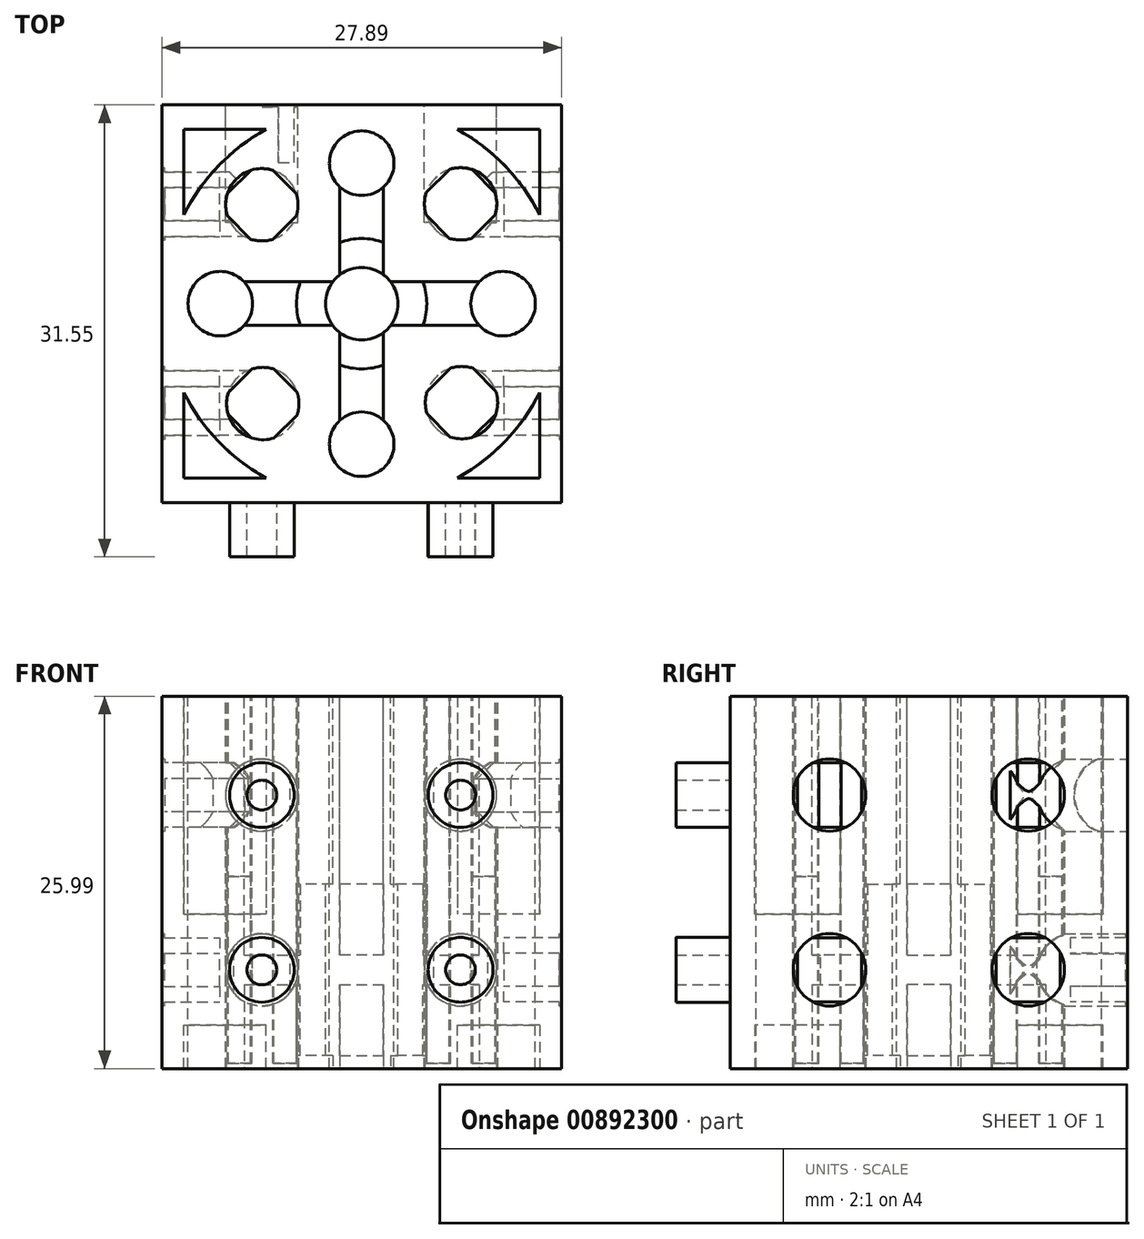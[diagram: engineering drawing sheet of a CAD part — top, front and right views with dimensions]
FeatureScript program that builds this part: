
annotation { "Feature Type Name" : "Feature", "Feature Type Description" : "" }
export const myFeature = defineFeature(function(context is Context, id is Id, definition is map)
    precondition{}
    {
        {
            var Q0;
            Q0=qCreatedBy(makeId("Top.planeOp"),FACE);
            var sketch = newSketch(context, id + "F0", { "sketchPlane" : qUnion([Q0])});
            skLineSegment(sketch, "E0.bottom", {"start": v(-12.61, 9.27) * mm, "end": v(15.28, 9.27) * mm});
            skLineSegment(sketch, "E0.top", {"start": v(-12.61, -18.5) * mm, "end": v(15.28, -18.5) * mm});
            skLineSegment(sketch, "E0.left", {"start": v(-12.61, 9.27) * mm, "end": v(-12.61, -18.5) * mm});
            skLineSegment(sketch, "E0.right", {"start": v(15.28, 9.27) * mm, "end": v(15.28, -18.5) * mm});
            skSolve(sketch);
        }
        {
            var Q0;
            Q0=qSketchRegion(id+"F0",true);
            extrude(context, id + "F1", {"entities" : qUnion([Q0]), "depth" : 13.8 * mm, "offsetDistance" : 25.4 * mm});
        }
        {
            var Q0;
            Q0=makeQuery(id+"F1.opExtrude","CAP_FACE",FACE,{"disambiguationData":[OSD([sQuery(id+"F0.wireOp",EDGE,"E0.bottom"),sQuery(id+"F0.wireOp",EDGE,"E0.top"),sQuery(id+"F0.wireOp",EDGE,"E0.left"),sQuery(id+"F0.wireOp",EDGE,"E0.right")])],"isStart":false});
            var sketch = newSketch(context, id + "F2", { "sketchPlane" : qUnion([Q0])});
            skLineSegment(sketch, "E1", {"start": v(1.33, 9.27) * mm, "end": v(1.33, -18.5) * mm, "construction": true});
            skLineSegment(sketch, "E2", {"start": v(-12.61, -4.61) * mm, "end": v(15.28, -4.61) * mm, "construction": true});
            skLineSegment(sketch, "E3.bottom", {"start": v(13.75, 7.56) * mm, "end": v(-11.09, 7.56) * mm});
            skLineSegment(sketch, "E3.top", {"start": v(13.75, -16.78) * mm, "end": v(-11.09, -16.78) * mm});
            skLineSegment(sketch, "E3.left", {"start": v(13.75, 7.56) * mm, "end": v(13.75, -16.78) * mm});
            skLineSegment(sketch, "E3.right", {"start": v(-11.09, 7.56) * mm, "end": v(-11.09, -16.78) * mm});
            skPoint(sketch, "E3.middle", {"position": v(1.33, -4.61) * mm});
            skSolve(sketch);
        }
        {
            var Q0;
            Q0=qSketchRegion(id+"F2",true);
            extrude(context, id + "F3", {"entities" : qUnion([Q0]), "operationType" : NewBodyOperationType.REMOVE, "oppositeDirection" : true, "depth" : 3.02 * mm, "offsetDistance" : 25.4 * mm});
        }
        {
            var Q0;
            Q0=makeQuery(id+"F1.opExtrude","CAP_FACE",FACE,{"disambiguationData":[OSD([sQuery(id+"F0.wireOp",EDGE,"E0.bottom"),sQuery(id+"F0.wireOp",EDGE,"E0.top"),sQuery(id+"F0.wireOp",EDGE,"E0.left"),sQuery(id+"F0.wireOp",EDGE,"E0.right")])],"isStart":true});
            var sketch = newSketch(context, id + "F4", { "sketchPlane" : qUnion([Q0])});
            skLineSegment(sketch, "E4.bottom", {"start": v(-11.09, -7.56) * mm, "end": v(13.75, -7.56) * mm});
            skLineSegment(sketch, "E4.top", {"start": v(-11.09, 16.78) * mm, "end": v(13.75, 16.78) * mm});
            skLineSegment(sketch, "E4.left", {"start": v(-11.09, -7.56) * mm, "end": v(-11.09, 16.78) * mm});
            skLineSegment(sketch, "E4.right", {"start": v(13.75, -7.56) * mm, "end": v(13.75, 16.78) * mm});
            skSolve(sketch);
        }
        {
            var Q0;
            Q0=makeQuery(id+"F4.imprint","IMPRINT",FACE,{"disambiguationData":[TD([[makeQuery(id+"F4.imprint","IMPRINT",EDGE,{"derivedFrom":sQuery(id+"F4.wireOp",EDGE,"E4.bottom")}),1.0]])]});
            extrude(context, id + "F5", {"entities" : qUnion([Q0]), "operationType" : NewBodyOperationType.REMOVE, "oppositeDirection" : true, "depth" : 3.02 * mm, "offsetDistance" : 25.4 * mm});
        }
        {
            var Q0;
            Q0=makeQuery(id+"F5.boolean.opBoolean","COPY",FACE,{"derivedFrom":makeQuery(id+"F5.opExtrude","CAP_FACE",FACE,{"disambiguationData":[OSD([sQuery(id+"F4.wireOp",EDGE,"E4.bottom"),sQuery(id+"F4.wireOp",EDGE,"E4.top"),sQuery(id+"F4.wireOp",EDGE,"E4.left"),sQuery(id+"F4.wireOp",EDGE,"E4.right")])],"isStart":false})});
            var sketch = newSketch(context, id + "F6", { "sketchPlane" : qUnion([Q0])});
            skCircle(sketch, "E5", {"center": v(1.33, 4.61) * mm, "radius": 13.88 * mm});
            skLineSegment(sketch, "E6", {"start": v(1.33, -7.56) * mm, "end": v(1.33, 16.78) * mm, "construction": true});
            skPoint(sketch, "E6.startSnap0", {"position": v(1.33, -7.56) * mm});
            skSolve(sketch);
        }
        {
            var Q0;
            {var subQ0=sQuery(id+"F6.wireOp",EDGE,"E5");var subQ1=makeQuery(id+"F5.boolean.opBoolean","COPY",EDGE,{"derivedFrom":makeQuery(id+"F5.opExtrude","CAP_EDGE",EDGE,{"disambiguationData":[OSD([sQuery(id+"F4.wireOp",EDGE,"E4.top")])],"isStart":false})});var subQ2=makeQuery(id+"F6.imprint","INTERSECT",VERTEX,{"disambiguationData":[OD(0.0)],"derivedFrom":[subQ1,subQ0]});Q0=makeQuery(id+"F6.imprint","IMPRINT",FACE,{"disambiguationData":[TD([[makeQuery(id+"F6.imprint","IMPRINT",EDGE,{"disambiguationData":[TD([[subQ2,-1.0]])],"derivedFrom":subQ0}),1.0]])]});}
            var Q1;
            {var subQ0=sQuery(id+"F6.wireOp",EDGE,"E5");var subQ1=makeQuery(id+"F5.boolean.opBoolean","COPY",EDGE,{"derivedFrom":makeQuery(id+"F5.opExtrude","CAP_EDGE",EDGE,{"disambiguationData":[OSD([sQuery(id+"F4.wireOp",EDGE,"E4.left")])],"isStart":false})});var subQ2=makeQuery(id+"F6.imprint","INTERSECT",VERTEX,{"disambiguationData":[OD(0.0)],"derivedFrom":[subQ1,subQ0]});Q1=makeQuery(id+"F6.imprint","IMPRINT",FACE,{"disambiguationData":[TD([[makeQuery(id+"F6.imprint","IMPRINT",EDGE,{"disambiguationData":[TD([[subQ2,-1.0]])],"derivedFrom":subQ0}),1.0]])]});}
            var Q2;
            {var subQ0=sQuery(id+"F6.wireOp",EDGE,"E5");var subQ1=makeQuery(id+"F5.boolean.opBoolean","COPY",EDGE,{"derivedFrom":makeQuery(id+"F5.opExtrude","CAP_EDGE",EDGE,{"disambiguationData":[OSD([sQuery(id+"F4.wireOp",EDGE,"E4.bottom")])],"isStart":false})});var subQ2=makeQuery(id+"F6.imprint","INTERSECT",VERTEX,{"disambiguationData":[OD(0.0)],"derivedFrom":[subQ1,subQ0]});Q2=makeQuery(id+"F6.imprint","IMPRINT",FACE,{"disambiguationData":[TD([[makeQuery(id+"F6.imprint","IMPRINT",EDGE,{"disambiguationData":[TD([[subQ2,-1.0]])],"derivedFrom":subQ0}),1.0]])]});}
            var Q3;
            {var subQ0=sQuery(id+"F6.wireOp",EDGE,"E5");var subQ1=makeQuery(id+"F5.boolean.opBoolean","COPY",EDGE,{"derivedFrom":makeQuery(id+"F5.opExtrude","CAP_EDGE",EDGE,{"disambiguationData":[OSD([sQuery(id+"F4.wireOp",EDGE,"E4.right")])],"isStart":false})});var subQ2=makeQuery(id+"F6.imprint","INTERSECT",VERTEX,{"disambiguationData":[OD(0.0)],"derivedFrom":[subQ1,subQ0]});Q3=makeQuery(id+"F6.imprint","IMPRINT",FACE,{"disambiguationData":[TD([[makeQuery(id+"F6.imprint","IMPRINT",EDGE,{"disambiguationData":[TD([[subQ2,1.0]])],"derivedFrom":subQ0}),1.0]])]});}
            var Q4;
            {var subQ0=sQuery(id+"F6.wireOp",EDGE,"E5");var subQ8=makeQuery(id+"F5.boolean.opBoolean","COPY",EDGE,{"derivedFrom":makeQuery(id+"F5.opExtrude","CAP_EDGE",EDGE,{"disambiguationData":[OSD([sQuery(id+"F4.wireOp",EDGE,"E4.top")])],"isStart":false})});var subQ11=makeQuery(id+"F6.imprint","INTERSECT",VERTEX,{"disambiguationData":[OD(0.0)],"derivedFrom":[subQ8,subQ0]});Q4=makeQuery(id+"F6.imprint","IMPRINT",FACE,{"disambiguationData":[TD([[makeQuery(id+"F6.imprint","IMPRINT",EDGE,{"disambiguationData":[TD([[subQ11,1.0]])],"derivedFrom":subQ0}),1.0]])]});}
            extrude(context, id + "F7", {"entities" : qUnion([Q0, Q1, Q2, Q3, Q4]), "operationType" : NewBodyOperationType.ADD, "depth" : 3.02 * mm, "offsetDistance" : 25.4 * mm});
        }
        {
            var Q0;
            Q0=makeQuery(id+"F3.boolean.opBoolean","COPY",FACE,{"derivedFrom":makeQuery(id+"F3.opExtrude","CAP_FACE",FACE,{"disambiguationData":[OSD([sQuery(id+"F2.wireOp",EDGE,"E3.bottom"),sQuery(id+"F2.wireOp",EDGE,"E3.top"),sQuery(id+"F2.wireOp",EDGE,"E3.left"),sQuery(id+"F2.wireOp",EDGE,"E3.right")])],"isStart":false})});
            var sketch = newSketch(context, id + "F8", { "sketchPlane" : qUnion([Q0])});
            skLineSegment(sketch, "E7", {"start": v(1.33, 7.56) * mm, "end": v(1.33, -16.78) * mm, "construction": true});
            skCircle(sketch, "E8", {"center": v(1.33, -4.61) * mm, "radius": 13.88 * mm});
            skSolve(sketch);
        }
        {
            var Q0;
            Q0=qSketchRegion(id+"F8",true);
            extrude(context, id + "F9", {"entities" : qUnion([Q0]), "operationType" : NewBodyOperationType.ADD, "depth" : 3.02 * mm, "offsetDistance" : 25.4 * mm});
        }
        {
            var Q0;
            Q0=makeQuery(id+"F9.boolean.opBoolean","MERGE",FACE,{"derivedFrom":[makeQuery(id+"F1.opExtrude","CAP_FACE",FACE,{"disambiguationData":[OSD([sQuery(id+"F0.wireOp",EDGE,"E0.bottom"),sQuery(id+"F0.wireOp",EDGE,"E0.top"),sQuery(id+"F0.wireOp",EDGE,"E0.left"),sQuery(id+"F0.wireOp",EDGE,"E0.right")])],"isStart":false}),makeQuery(id+"F9.opExtrude","CAP_FACE",FACE,{"disambiguationData":[OSD([sQuery(id+"F8.wireOp",EDGE,"E8")])],"isStart":false})]});
            var sketch = newSketch(context, id + "F10", { "sketchPlane" : qUnion([Q0])});
            skLineSegment(sketch, "E9", {"start": v(-12.61, -4.61) * mm, "end": v(15.28, -4.61) * mm, "construction": true});
            skLineSegment(sketch, "E10", {"start": v(1.33, 9.27) * mm, "end": v(1.33, -18.5) * mm, "construction": true});
            skCircle(sketch, "E11", {"center": v(1.33, -4.61) * mm, "radius": 2.53 * mm});
            skCircle(sketch, "E12", {"center": v(1.33, -14.42) * mm, "radius": 2.25 * mm});
            skCircle(sketch, "E13", {"center": v(1.33, 5.2) * mm, "radius": 2.25 * mm});
            skCircle(sketch, "E14", {"center": v(-8.54, -4.61) * mm, "radius": 2.25 * mm});
            skCircle(sketch, "E15", {"center": v(11.2, -4.61) * mm, "radius": 2.25 * mm});
            skCircle(sketch, "E16", {"center": v(-5.64, 2.3) * mm, "radius": 2.53 * mm});
            skCircle(sketch, "E17.1.0", {"center": v(-5.57, -11.58) * mm, "radius": 2.53 * mm});
            skCircle(sketch, "E17.2.0", {"center": v(8.3, -11.52) * mm, "radius": 2.53 * mm});
            skCircle(sketch, "E17.3.0", {"center": v(8.24, 2.36) * mm, "radius": 2.53 * mm});
            skSolve(sketch);
        }
        {
            var Q0;
            Q0=qSketchRegion(id+"F10",true);
            extrude(context, id + "F11", {"entities" : qUnion([Q0]), "operationType" : NewBodyOperationType.REMOVE, "oppositeDirection" : true, "depth" : 25.4 * mm, "offsetDistance" : 25.4 * mm});
        }
        {
            var Q0;
            Q0=makeQuery(id+"F9.boolean.opBoolean","MERGE",FACE,{"derivedFrom":[makeQuery(id+"F1.opExtrude","CAP_FACE",FACE,{"disambiguationData":[OSD([sQuery(id+"F0.wireOp",EDGE,"E0.bottom"),sQuery(id+"F0.wireOp",EDGE,"E0.top"),sQuery(id+"F0.wireOp",EDGE,"E0.left"),sQuery(id+"F0.wireOp",EDGE,"E0.right")])],"isStart":false}),makeQuery(id+"F9.opExtrude","CAP_FACE",FACE,{"disambiguationData":[OSD([sQuery(id+"F8.wireOp",EDGE,"E8")])],"isStart":false})]});
            var sketch = newSketch(context, id + "F12", { "sketchPlane" : qUnion([Q0])});
            skLineSegment(sketch, "E18", {"start": v(-12.61, -4.61) * mm, "end": v(15.28, -4.61) * mm, "construction": true});
            skLineSegment(sketch, "E19", {"start": v(1.33, 9.27) * mm, "end": v(1.33, -18.5) * mm, "construction": true});
            skLineSegment(sketch, "E20", {"start": v(-6.88, -3.09) * mm, "end": v(9.55, -3.09) * mm});
            skLineSegment(sketch, "E21", {"start": v(-6.88, -6.14) * mm, "end": v(9.55, -6.14) * mm});
            skLineSegment(sketch, "E22", {"start": v(-0.19, 3.54) * mm, "end": v(-0.19, -12.76) * mm});
            skLineSegment(sketch, "E23", {"start": v(2.86, -12.76) * mm, "end": v(2.86, 3.54) * mm});
            skLineSegment(sketch, "E24", {"start": v(-0.19, -7.96) * mm, "end": v(2.86, -7.96) * mm, "construction": true});
            skPoint(sketch, "E25", {"position": v(1.33, -7.96) * mm});
            skLineSegment(sketch, "E26", {"start": v(-2, -3.09) * mm, "end": v(-2, -6.14) * mm, "construction": true});
            skPoint(sketch, "E27", {"position": v(-2, -4.61) * mm});
            skSolve(sketch);
        }
        {
            var Q0;
            {var subQ0=sQuery(id+"F12.wireOp",EDGE,"E22");var subQ1=makeQuery(id+"F11.boolean.opBoolean","COPY",EDGE,{"derivedFrom":makeQuery(id+"F11.opExtrude","CAP_EDGE",EDGE,{"disambiguationData":[OSD([sQuery(id+"F10.wireOp",EDGE,"E13")])],"isStart":true})});var subQ2=makeQuery(id+"F12.imprint","INTERSECT",VERTEX,{"derivedFrom":[subQ1,subQ0]});Q0=makeQuery(id+"F12.imprint","IMPRINT",FACE,{"disambiguationData":[TD([[makeQuery(id+"F12.imprint","IMPRINT",EDGE,{"disambiguationData":[TD([[subQ2,-1.0]])],"derivedFrom":subQ0}),1.0]])]});}
            var Q1;
            {var subQ0=sQuery(id+"F12.wireOp",EDGE,"E22");var subQ1=makeQuery(id+"F11.boolean.opBoolean","COPY",EDGE,{"derivedFrom":makeQuery(id+"F11.opExtrude","CAP_EDGE",EDGE,{"disambiguationData":[OSD([sQuery(id+"F10.wireOp",EDGE,"E12")])],"isStart":true})});var subQ2=makeQuery(id+"F12.imprint","INTERSECT",VERTEX,{"derivedFrom":[subQ1,subQ0]});Q1=makeQuery(id+"F12.imprint","IMPRINT",FACE,{"disambiguationData":[TD([[makeQuery(id+"F12.imprint","IMPRINT",EDGE,{"disambiguationData":[TD([[subQ2,1.0]])],"derivedFrom":subQ0}),1.0]])]});}
            var Q2;
            {var subQ0=sQuery(id+"F12.wireOp",EDGE,"E20");var subQ1=makeQuery(id+"F11.boolean.opBoolean","COPY",EDGE,{"derivedFrom":makeQuery(id+"F11.opExtrude","CAP_EDGE",EDGE,{"disambiguationData":[OSD([sQuery(id+"F10.wireOp",EDGE,"E14")])],"isStart":true})});var subQ2=makeQuery(id+"F12.imprint","INTERSECT",VERTEX,{"derivedFrom":[subQ1,subQ0]});Q2=makeQuery(id+"F12.imprint","IMPRINT",FACE,{"disambiguationData":[TD([[makeQuery(id+"F12.imprint","IMPRINT",EDGE,{"disambiguationData":[TD([[subQ2,-1.0]])],"derivedFrom":subQ0}),-1.0]])]});}
            var Q3;
            {var subQ0=sQuery(id+"F12.wireOp",EDGE,"E20");var subQ1=makeQuery(id+"F11.boolean.opBoolean","COPY",EDGE,{"derivedFrom":makeQuery(id+"F11.opExtrude","CAP_EDGE",EDGE,{"disambiguationData":[OSD([sQuery(id+"F10.wireOp",EDGE,"E15")])],"isStart":true})});var subQ2=makeQuery(id+"F12.imprint","INTERSECT",VERTEX,{"derivedFrom":[subQ1,subQ0]});Q3=makeQuery(id+"F12.imprint","IMPRINT",FACE,{"disambiguationData":[TD([[makeQuery(id+"F12.imprint","IMPRINT",EDGE,{"disambiguationData":[TD([[subQ2,1.0]])],"derivedFrom":subQ0}),-1.0]])]});}
            extrude(context, id + "F13", {"entities" : qUnion([Q0, Q1, Q2, Q3]), "operationType" : NewBodyOperationType.REMOVE, "oppositeDirection" : true, "depth" : 5.87 * mm, "offsetDistance" : 25.4 * mm});
        }
        {
            var Q0;
            Q0=makeQuery(id+"F7.boolean.opBoolean","MERGE",FACE,{"derivedFrom":[makeQuery(id+"F1.opExtrude","CAP_FACE",FACE,{"disambiguationData":[OSD([sQuery(id+"F0.wireOp",EDGE,"E0.bottom"),sQuery(id+"F0.wireOp",EDGE,"E0.top"),sQuery(id+"F0.wireOp",EDGE,"E0.left"),sQuery(id+"F0.wireOp",EDGE,"E0.right")])],"isStart":true}),makeQuery(id+"F7.opExtrude","CAP_FACE",FACE,{"disambiguationData":[OSD([sQuery(id+"F6.wireOp",EDGE,"E5")])],"isStart":false})]});
            var sketch = newSketch(context, id + "F14", { "sketchPlane" : qUnion([Q0])});
            skLineSegment(sketch, "E28.0", {"start": v(2.86, 12.76) * mm, "end": v(2.86, 6.63) * mm});
            skLineSegment(sketch, "E28.1", {"start": v(3.35, 6.14) * mm, "end": v(9.55, 6.14) * mm});
            skLineSegment(sketch, "E28.2", {"start": v(3.35, 3.09) * mm, "end": v(9.55, 3.09) * mm});
            skLineSegment(sketch, "E28.3", {"start": v(2.86, 2.6) * mm, "end": v(2.86, -3.54) * mm});
            skLineSegment(sketch, "E28.4", {"start": v(-0.19, -3.54) * mm, "end": v(-0.19, 2.6) * mm});
            skLineSegment(sketch, "E28.5", {"start": v(-0.19, 6.63) * mm, "end": v(-0.19, 12.76) * mm});
            skLineSegment(sketch, "E28.6", {"start": v(-6.88, 6.14) * mm, "end": v(-0.68, 6.14) * mm});
            skLineSegment(sketch, "E28.7", {"start": v(-6.88, 3.09) * mm, "end": v(-0.68, 3.09) * mm});
            skSolve(sketch);
        }
        {
            var Q0;
            {var subQ0=sQuery(id+"F14.wireOp",EDGE,"E28.6");Q0=makeQuery(id+"F14.imprint","IMPRINT",FACE,{"disambiguationData":[TD([[makeQuery(id+"F14.imprint","IMPRINT",EDGE,{"derivedFrom":subQ0}),-1.0]])]});}
            var Q1;
            {var subQ0=sQuery(id+"F14.wireOp",EDGE,"E28.3");Q1=makeQuery(id+"F14.imprint","IMPRINT",FACE,{"disambiguationData":[TD([[makeQuery(id+"F14.imprint","IMPRINT",EDGE,{"derivedFrom":subQ0}),-1.0]])]});}
            var Q2;
            {var subQ0=sQuery(id+"F14.wireOp",EDGE,"E28.0");Q2=makeQuery(id+"F14.imprint","IMPRINT",FACE,{"disambiguationData":[TD([[makeQuery(id+"F14.imprint","IMPRINT",EDGE,{"derivedFrom":subQ0}),-1.0]])]});}
            var Q3;
            {var subQ0=sQuery(id+"F14.wireOp",EDGE,"E28.1");Q3=makeQuery(id+"F14.imprint","IMPRINT",FACE,{"disambiguationData":[TD([[makeQuery(id+"F14.imprint","IMPRINT",EDGE,{"derivedFrom":subQ0}),-1.0]])]});}
            extrude(context, id + "F15", {"entities" : qUnion([Q0, Q1, Q2, Q3]), "operationType" : NewBodyOperationType.REMOVE, "oppositeDirection" : true, "depth" : 5.87 * mm, "offsetDistance" : 25.4 * mm});
        }
        {
            var Q0;
            Q0=makeQuery(id+"F15.boolean.opBoolean","COPY",FACE,{"derivedFrom":makeQuery(id+"F15.opExtrude","CAP_FACE",FACE,{"disambiguationData":[OSD([sQuery(id+"F0.wireOp",EDGE,"E0.bottom"),sQuery(id+"F0.wireOp",EDGE,"E0.top"),sQuery(id+"F0.wireOp",EDGE,"E0.left"),sQuery(id+"F0.wireOp",EDGE,"E0.right"),sQuery(id+"F6.wireOp",EDGE,"E5"),sQuery(id+"F10.wireOp",EDGE,"E11"),sQuery(id+"F10.wireOp",EDGE,"E13"),sQuery(id+"F14.wireOp",EDGE,"E28.3"),sQuery(id+"F14.wireOp",EDGE,"E28.4")])],"isStart":false})});
            var sketch = newSketch(context, id + "F16", { "sketchPlane" : qUnion([Q0])});
            skCircle(sketch, "E29", {"center": v(1.33, 4.61) * mm, "radius": 4.55 * mm});
            skCircle(sketch, "E30", {"center": v(1.33, 4.61) * mm, "radius": 2.53 * mm});
            skSolve(sketch);
        }
        {
            var Q0;
            {var subQ5=sQuery(id+"F16.wireOp",EDGE,"E30");Q0=makeQuery(id+"F16.imprint","IMPRINT",FACE,{"disambiguationData":[TD([[makeQuery(id+"F16.imprint","IMPRINT",EDGE,{"disambiguationData":[OD(1.0)],"derivedFrom":subQ5}),-1.0]])]});}
            var Q1;
            {var subQ5=sQuery(id+"F16.wireOp",EDGE,"E30");Q1=makeQuery(id+"F16.imprint","IMPRINT",FACE,{"disambiguationData":[TD([[makeQuery(id+"F16.imprint","IMPRINT",EDGE,{"disambiguationData":[OD(0.0)],"derivedFrom":subQ5}),1.0]])]});}
            extrude(context, id + "F17", {"entities" : qUnion([Q0, Q1]), "operationType" : NewBodyOperationType.ADD, "depth" : 4.95 * mm, "offsetDistance" : 25.4 * mm});
        }
        {
            var Q0;
            Q0=makeQuery(id+"F13.boolean.opBoolean","COPY",FACE,{"derivedFrom":makeQuery(id+"F13.opExtrude","CAP_FACE",FACE,{"disambiguationData":[OSD([sQuery(id+"F10.wireOp",EDGE,"E11"),sQuery(id+"F10.wireOp",EDGE,"E12"),sQuery(id+"F12.wireOp",EDGE,"E22"),sQuery(id+"F12.wireOp",EDGE,"E23")])],"isStart":false})});
            var sketch = newSketch(context, id + "F18", { "sketchPlane" : qUnion([Q0])});
            skCircle(sketch, "E31", {"center": v(1.33, -4.61) * mm, "radius": 4.55 * mm});
            skCircle(sketch, "E32", {"center": v(1.33, -4.61) * mm, "radius": 2.53 * mm});
            skSolve(sketch);
        }
        {
            var Q0;
            {var subQ0=sQuery(id+"F18.wireOp",EDGE,"E31");var subQ1=sQuery(id+"F12.wireOp",EDGE,"E22");var subQ2=makeQuery(id+"F11.boolean.opBoolean","COPY",EDGE,{"derivedFrom":makeQuery(id+"F11.opExtrude","CAP_EDGE",EDGE,{"disambiguationData":[OSD([sQuery(id+"F10.wireOp",EDGE,"E12")])],"isStart":true})});var subQ4=makeQuery(id+"F13.boolean.opBoolean","COPY",EDGE,{"derivedFrom":makeQuery(id+"F13.opExtrude","CAP_EDGE",EDGE,{"disambiguationData":[OSD([subQ1]),TDD([makeQuery(id+"F12.imprint","IMPRINT",EDGE,{"disambiguationData":[TD([[makeQuery(id+"F12.imprint","INTERSECT",VERTEX,{"derivedFrom":[subQ2,subQ1]}),1.0]])],"derivedFrom":subQ1})])],"isStart":false})});var subQ5=makeQuery(id+"F18.imprint","INTERSECT",VERTEX,{"derivedFrom":[subQ4,subQ0]});Q0=makeQuery(id+"F18.imprint","IMPRINT",FACE,{"disambiguationData":[TD([[makeQuery(id+"F18.imprint","IMPRINT",EDGE,{"disambiguationData":[TD([[subQ5,1.0]])],"derivedFrom":subQ0}),1.0]])]});}
            var Q1;
            {var subQ0=sQuery(id+"F18.wireOp",EDGE,"E31");var subQ1=sQuery(id+"F12.wireOp",EDGE,"E22");var subQ2=makeQuery(id+"F11.boolean.opBoolean","COPY",EDGE,{"derivedFrom":makeQuery(id+"F11.opExtrude","CAP_EDGE",EDGE,{"disambiguationData":[OSD([sQuery(id+"F10.wireOp",EDGE,"E12")])],"isStart":true})});var subQ4=makeQuery(id+"F13.boolean.opBoolean","COPY",EDGE,{"derivedFrom":makeQuery(id+"F13.opExtrude","CAP_EDGE",EDGE,{"disambiguationData":[OSD([subQ1]),TDD([makeQuery(id+"F12.imprint","IMPRINT",EDGE,{"disambiguationData":[TD([[makeQuery(id+"F12.imprint","INTERSECT",VERTEX,{"derivedFrom":[subQ2,subQ1]}),1.0]])],"derivedFrom":subQ1})])],"isStart":false})});var subQ5=makeQuery(id+"F18.imprint","INTERSECT",VERTEX,{"derivedFrom":[subQ4,subQ0]});Q1=makeQuery(id+"F18.imprint","IMPRINT",FACE,{"disambiguationData":[TD([[makeQuery(id+"F18.imprint","IMPRINT",EDGE,{"disambiguationData":[TD([[subQ5,-1.0]])],"derivedFrom":subQ0}),1.0]])]});}
            extrude(context, id + "F19", {"entities" : qUnion([Q0, Q1]), "operationType" : NewBodyOperationType.ADD, "depth" : 4.95 * mm, "offsetDistance" : 25.4 * mm});
        }
        {
            var Q0;
            Q0=makeQuery(id+"F1.opExtrude","SWEPT_FACE",FACE,{"disambiguationData":[OSD([sQuery(id+"F0.wireOp",EDGE,"E0.top")])]});
            var sketch = newSketch(context, id + "F20", { "sketchPlane" : qUnion([Q0])});
            skLineSegment(sketch, "E33", {"start": v(15.28, 6.9) * mm, "end": v(-12.61, 6.9) * mm, "construction": true});
            skCircle(sketch, "E34", {"center": v(8.23, 6.9) * mm, "radius": 2.26 * mm});
            skCircle(sketch, "E35", {"center": v(-5.64, 6.9) * mm, "radius": 2.26 * mm});
            skLineSegment(sketch, "E36", {"start": v(1.33, 0) * mm, "end": v(1.33, 13.8) * mm, "construction": true});
            skPoint(sketch, "E37", {"position": v(1.33, 6.9) * mm});
            skLineSegment(sketch, "E38", {"start": v(1.33, 0) * mm, "end": v(15.28, 0) * mm, "construction": true});
            skLineSegment(sketch, "E39", {"start": v(15.28, 0) * mm, "end": v(8.3, 0) * mm});
            skLineSegment(sketch, "E40", {"start": v(8.3, 0) * mm, "end": v(8.3, 13.8) * mm, "construction": true});
            skLineSegment(sketch, "E41", {"start": v(1.33, 0) * mm, "end": v(-12.61, 0) * mm, "construction": true});
            skLineSegment(sketch, "E42", {"start": v(-5.64, 0) * mm, "end": v(-5.64, 13.8) * mm, "construction": true});
            skCircle(sketch, "E43", {"center": v(8.23, 6.9) * mm, "radius": 1.04 * mm});
            skCircle(sketch, "E44", {"center": v(-5.64, 6.9) * mm, "radius": 1.04 * mm});
            skLineSegment(sketch, "E45.0", {"start": v(-12.61, 13.8) * mm, "end": v(-12.61, 0) * mm});
            skSolve(sketch);
        }
        {
            var Q0;
            Q0=makeQuery(id+"F20.imprint","IMPRINT",FACE,{"disambiguationData":[TD([[makeQuery(id+"F20.imprint","IMPRINT",EDGE,{"derivedFrom":sQuery(id+"F20.wireOp",EDGE,"E34")}),1.0]])]});
            var Q1;
            Q1=makeQuery(id+"F20.imprint","IMPRINT",FACE,{"disambiguationData":[TD([[makeQuery(id+"F20.imprint","IMPRINT",EDGE,{"derivedFrom":sQuery(id+"F20.wireOp",EDGE,"E35")}),1.0]])]});
            extrude(context, id + "F21", {"entities" : qUnion([Q0, Q1]), "operationType" : NewBodyOperationType.ADD, "depth" : 3.78 * mm, "offsetDistance" : 25.4 * mm});
        }
        {
            var Q0;
            Q0=makeQuery(id+"F1.opExtrude","SWEPT_FACE",FACE,{"disambiguationData":[OSD([sQuery(id+"F0.wireOp",EDGE,"E0.bottom")])]});
            var sketch = newSketch(context, id + "F22", { "sketchPlane" : qUnion([Q0])});
            skCircle(sketch, "E46.0", {"center": v(-8.23, 6.9) * mm, "radius": 2.26 * mm, "construction": true});
            skCircle(sketch, "E46.1", {"center": v(5.64, 6.9) * mm, "radius": 2.26 * mm, "construction": true});
            skCircle(sketch, "E47", {"center": v(-8.23, 6.9) * mm, "radius": 2.53 * mm});
            skCircle(sketch, "E48", {"center": v(5.64, 6.9) * mm, "radius": 2.53 * mm});
            skSolve(sketch);
        }
        {
            var Q0;
            Q0=qSketchRegion(id+"F22",true);
            extrude(context, id + "F23", {"entities" : qUnion([Q0]), "operationType" : NewBodyOperationType.REMOVE, "oppositeDirection" : true, "depth" : 4 * mm, "offsetDistance" : 25.4 * mm});
        }
        {
            var Q0;
            Q0=makeQuery(id+"F1.opExtrude","SWEPT_FACE",FACE,{"disambiguationData":[OSD([sQuery(id+"F0.wireOp",EDGE,"E0.right")])]});
            var sketch = newSketch(context, id + "F24", { "sketchPlane" : qUnion([Q0])});
            skLineSegment(sketch, "E49", {"start": v(9.27, 6.9) * mm, "end": v(-18.5, 6.9) * mm, "construction": true});
            skLineSegment(sketch, "E50", {"start": v(-4.61, 13.8) * mm, "end": v(-4.61, 0) * mm});
            skLineSegment(sketch, "E51", {"start": v(-4.61, 13.8) * mm, "end": v(9.27, 13.8) * mm, "construction": true});
            skLineSegment(sketch, "E52", {"start": v(-4.61, 13.8) * mm, "end": v(-18.5, 13.8) * mm, "construction": true});
            skLineSegment(sketch, "E53", {"start": v(-11.55, 13.8) * mm, "end": v(-11.55, 0) * mm, "construction": true});
            skLineSegment(sketch, "E54", {"start": v(2.33, 13.8) * mm, "end": v(2.33, 0) * mm, "construction": true});
            skPoint(sketch, "E55", {"position": v(-11.55, 6.9) * mm});
            skPoint(sketch, "E56", {"position": v(2.33, 6.9) * mm});
            skCircle(sketch, "E57", {"center": v(-11.55, 6.9) * mm, "radius": 2.53 * mm});
            skCircle(sketch, "E58", {"center": v(2.33, 6.9) * mm, "radius": 2.53 * mm});
            skSolve(sketch);
        }
        {
            var Q0;
            Q0=qSketchRegion(id+"F24",true);
            extrude(context, id + "F25", {"entities" : qUnion([Q0]), "operationType" : NewBodyOperationType.REMOVE, "oppositeDirection" : true, "depth" : 4 * mm, "offsetDistance" : 25.4 * mm});
        }
        {
            var Q0;
            Q0=makeQuery(id+"F1.opExtrude","SWEPT_FACE",FACE,{"disambiguationData":[OSD([sQuery(id+"F0.wireOp",EDGE,"E0.left")])]});
            var sketch = newSketch(context, id + "F26", { "sketchPlane" : qUnion([Q0])});
            skCircle(sketch, "E59.0", {"center": v(-2.33, 6.9) * mm, "radius": 2.53 * mm});
            skCircle(sketch, "E59.1", {"center": v(11.55, 6.9) * mm, "radius": 2.53 * mm});
            skSolve(sketch);
        }
        {
            var Q0;
            Q0=qSketchRegion(id+"F26",true);
            extrude(context, id + "F27", {"entities" : qUnion([Q0]), "operationType" : NewBodyOperationType.REMOVE, "oppositeDirection" : true, "depth" : 4 * mm, "offsetDistance" : 25.4 * mm});
        }
        {
            var Q0;
            Q0=makeQuery(id+"F23.boolean.opBoolean","COPY",FACE,{"derivedFrom":makeQuery(id+"F23.opExtrude","CAP_FACE",FACE,{"disambiguationData":[OSD([sQuery(id+"F22.wireOp",EDGE,"E47")])],"isStart":false})});
            var sketch = newSketch(context, id + "F28", { "sketchPlane" : qUnion([Q0])});
            skLineSegment(sketch, "E60.bottom", {"start": v(-5.98, 9.14) * mm, "end": v(-10.48, 9.14) * mm});
            skLineSegment(sketch, "E60.top", {"start": v(-5.98, 4.65) * mm, "end": v(-10.48, 4.65) * mm});
            skLineSegment(sketch, "E60.left", {"start": v(-5.98, 9.14) * mm, "end": v(-5.98, 4.65) * mm});
            skLineSegment(sketch, "E60.right", {"start": v(-10.48, 9.14) * mm, "end": v(-10.48, 4.65) * mm});
            skPoint(sketch, "E60.middle", {"position": v(-8.23, 6.9) * mm});
            skLineSegment(sketch, "E61.bottom", {"start": v(7.89, 9.14) * mm, "end": v(3.4, 9.14) * mm});
            skLineSegment(sketch, "E61.top", {"start": v(7.89, 4.65) * mm, "end": v(3.4, 4.65) * mm});
            skLineSegment(sketch, "E61.left", {"start": v(7.89, 9.14) * mm, "end": v(7.89, 4.65) * mm});
            skLineSegment(sketch, "E61.right", {"start": v(3.4, 9.14) * mm, "end": v(3.4, 4.65) * mm});
            skPoint(sketch, "E61.middle", {"position": v(5.64, 6.9) * mm});
            skCircle(sketch, "E62.0", {"center": v(-8.23, 6.9) * mm, "radius": 2.53 * mm});
            skCircle(sketch, "E63.0", {"center": v(5.64, 6.9) * mm, "radius": 2.53 * mm});
            skSolve(sketch);
        }
        {
            var Q0;
            {var subQ0=sQuery(id+"F28.wireOp",EDGE,"E62.0");var subQ1=sQuery(id+"F28.wireOp",EDGE,"E60.right");var subQ2=makeQuery(id+"F28.imprint","INTERSECT",VERTEX,{"disambiguationData":[OD(0.0)],"derivedFrom":[subQ1,subQ0]});Q0=makeQuery(id+"F28.imprint","IMPRINT",FACE,{"disambiguationData":[TD([[makeQuery(id+"F28.imprint","IMPRINT",EDGE,{"disambiguationData":[TD([[subQ2,-1.0]])],"derivedFrom":subQ1}),-1.0]])]});}
            var Q1;
            {var subQ0=sQuery(id+"F28.wireOp",EDGE,"E62.0");var subQ1=sQuery(id+"F28.wireOp",EDGE,"E60.top");var subQ2=makeQuery(id+"F28.imprint","INTERSECT",VERTEX,{"disambiguationData":[OD(0.0)],"derivedFrom":[subQ1,subQ0]});Q1=makeQuery(id+"F28.imprint","IMPRINT",FACE,{"disambiguationData":[TD([[makeQuery(id+"F28.imprint","IMPRINT",EDGE,{"disambiguationData":[TD([[subQ2,-1.0]])],"derivedFrom":subQ1}),1.0]])]});}
            var Q2;
            {var subQ0=sQuery(id+"F28.wireOp",EDGE,"E62.0");var subQ1=sQuery(id+"F28.wireOp",EDGE,"E60.left");var subQ2=makeQuery(id+"F28.imprint","INTERSECT",VERTEX,{"disambiguationData":[OD(0.0)],"derivedFrom":[subQ1,subQ0]});Q2=makeQuery(id+"F28.imprint","IMPRINT",FACE,{"disambiguationData":[TD([[makeQuery(id+"F28.imprint","IMPRINT",EDGE,{"disambiguationData":[TD([[subQ2,-1.0]])],"derivedFrom":subQ1}),1.0]])]});}
            var Q3;
            {var subQ0=sQuery(id+"F28.wireOp",EDGE,"E62.0");var subQ1=sQuery(id+"F28.wireOp",EDGE,"E60.bottom");var subQ2=makeQuery(id+"F28.imprint","INTERSECT",VERTEX,{"disambiguationData":[OD(0.0)],"derivedFrom":[subQ1,subQ0]});Q3=makeQuery(id+"F28.imprint","IMPRINT",FACE,{"disambiguationData":[TD([[makeQuery(id+"F28.imprint","IMPRINT",EDGE,{"disambiguationData":[TD([[subQ2,-1.0]])],"derivedFrom":subQ1}),-1.0]])]});}
            var Q4;
            {var subQ0=sQuery(id+"F28.wireOp",EDGE,"E63.0");var subQ1=sQuery(id+"F28.wireOp",EDGE,"E61.bottom");var subQ2=makeQuery(id+"F28.imprint","INTERSECT",VERTEX,{"disambiguationData":[OD(0.0)],"derivedFrom":[subQ1,subQ0]});Q4=makeQuery(id+"F28.imprint","IMPRINT",FACE,{"disambiguationData":[TD([[makeQuery(id+"F28.imprint","IMPRINT",EDGE,{"disambiguationData":[TD([[subQ2,-1.0]])],"derivedFrom":subQ1}),-1.0]])]});}
            var Q5;
            {var subQ0=sQuery(id+"F28.wireOp",EDGE,"E63.0");var subQ1=sQuery(id+"F28.wireOp",EDGE,"E61.left");var subQ2=makeQuery(id+"F28.imprint","INTERSECT",VERTEX,{"disambiguationData":[OD(0.0)],"derivedFrom":[subQ1,subQ0]});Q5=makeQuery(id+"F28.imprint","IMPRINT",FACE,{"disambiguationData":[TD([[makeQuery(id+"F28.imprint","IMPRINT",EDGE,{"disambiguationData":[TD([[subQ2,-1.0]])],"derivedFrom":subQ1}),1.0]])]});}
            var Q6;
            {var subQ0=sQuery(id+"F28.wireOp",EDGE,"E63.0");var subQ1=sQuery(id+"F28.wireOp",EDGE,"E61.right");var subQ2=makeQuery(id+"F28.imprint","INTERSECT",VERTEX,{"disambiguationData":[OD(0.0)],"derivedFrom":[subQ1,subQ0]});Q6=makeQuery(id+"F28.imprint","IMPRINT",FACE,{"disambiguationData":[TD([[makeQuery(id+"F28.imprint","IMPRINT",EDGE,{"disambiguationData":[TD([[subQ2,-1.0]])],"derivedFrom":subQ1}),-1.0]])]});}
            var Q7;
            {var subQ0=sQuery(id+"F28.wireOp",EDGE,"E63.0");var subQ1=sQuery(id+"F28.wireOp",EDGE,"E61.top");var subQ2=makeQuery(id+"F28.imprint","INTERSECT",VERTEX,{"disambiguationData":[OD(0.0)],"derivedFrom":[subQ1,subQ0]});Q7=makeQuery(id+"F28.imprint","IMPRINT",FACE,{"disambiguationData":[TD([[makeQuery(id+"F28.imprint","IMPRINT",EDGE,{"disambiguationData":[TD([[subQ2,-1.0]])],"derivedFrom":subQ1}),1.0]])]});}
            extrude(context, id + "F29", {"entities" : qUnion([Q0, Q1, Q2, Q3, Q4, Q5, Q6, Q7]), "operationType" : NewBodyOperationType.ADD, "depth" : 3.86 * mm, "offsetDistance" : 25.4 * mm});
        }
        {
            var Q0;
            Q0=makeQuery(id+"F25.boolean.opBoolean","COPY",FACE,{"derivedFrom":makeQuery(id+"F25.opExtrude","CAP_FACE",FACE,{"disambiguationData":[OSD([sQuery(id+"F24.wireOp",EDGE,"E57")])],"isStart":false})});
            var sketch = newSketch(context, id + "F30", { "sketchPlane" : qUnion([Q0])});
            skLineSegment(sketch, "E64.bottom", {"start": v(-9.3, 9.14) * mm, "end": v(-13.8, 9.14) * mm});
            skLineSegment(sketch, "E64.top", {"start": v(-9.3, 4.65) * mm, "end": v(-13.8, 4.65) * mm});
            skLineSegment(sketch, "E64.left", {"start": v(-9.3, 9.14) * mm, "end": v(-9.3, 4.65) * mm});
            skLineSegment(sketch, "E64.right", {"start": v(-13.8, 9.14) * mm, "end": v(-13.8, 4.65) * mm});
            skPoint(sketch, "E64.middle", {"position": v(-11.55, 6.9) * mm});
            skLineSegment(sketch, "E65.bottom", {"start": v(4.58, 9.14) * mm, "end": v(0.08, 9.14) * mm});
            skLineSegment(sketch, "E65.top", {"start": v(4.58, 4.65) * mm, "end": v(0.08, 4.65) * mm});
            skLineSegment(sketch, "E65.left", {"start": v(4.58, 9.14) * mm, "end": v(4.58, 4.65) * mm});
            skLineSegment(sketch, "E65.right", {"start": v(0.08, 9.14) * mm, "end": v(0.08, 4.65) * mm});
            skPoint(sketch, "E65.middle", {"position": v(2.33, 6.9) * mm});
            skCircle(sketch, "E66.0", {"center": v(-11.55, 6.9) * mm, "radius": 2.53 * mm});
            skCircle(sketch, "E66.1", {"center": v(2.33, 6.9) * mm, "radius": 2.53 * mm});
            skSolve(sketch);
        }
        {
            var Q0;
            {var subQ0=sQuery(id+"F30.wireOp",EDGE,"E66.0");var subQ1=sQuery(id+"F30.wireOp",EDGE,"E64.bottom");var subQ2=makeQuery(id+"F30.imprint","INTERSECT",VERTEX,{"disambiguationData":[OD(0.0)],"derivedFrom":[subQ1,subQ0]});Q0=makeQuery(id+"F30.imprint","IMPRINT",FACE,{"disambiguationData":[TD([[makeQuery(id+"F30.imprint","IMPRINT",EDGE,{"disambiguationData":[TD([[subQ2,-1.0]])],"derivedFrom":subQ1}),-1.0]])]});}
            var Q1;
            {var subQ0=sQuery(id+"F30.wireOp",EDGE,"E66.0");var subQ1=sQuery(id+"F30.wireOp",EDGE,"E64.right");var subQ2=makeQuery(id+"F30.imprint","INTERSECT",VERTEX,{"disambiguationData":[OD(0.0)],"derivedFrom":[subQ1,subQ0]});Q1=makeQuery(id+"F30.imprint","IMPRINT",FACE,{"disambiguationData":[TD([[makeQuery(id+"F30.imprint","IMPRINT",EDGE,{"disambiguationData":[TD([[subQ2,-1.0]])],"derivedFrom":subQ1}),-1.0]])]});}
            var Q2;
            {var subQ0=sQuery(id+"F30.wireOp",EDGE,"E66.0");var subQ1=sQuery(id+"F30.wireOp",EDGE,"E64.left");var subQ2=makeQuery(id+"F30.imprint","INTERSECT",VERTEX,{"disambiguationData":[OD(0.0)],"derivedFrom":[subQ1,subQ0]});Q2=makeQuery(id+"F30.imprint","IMPRINT",FACE,{"disambiguationData":[TD([[makeQuery(id+"F30.imprint","IMPRINT",EDGE,{"disambiguationData":[TD([[subQ2,-1.0]])],"derivedFrom":subQ1}),1.0]])]});}
            var Q3;
            {var subQ0=sQuery(id+"F30.wireOp",EDGE,"E66.0");var subQ1=sQuery(id+"F30.wireOp",EDGE,"E64.top");var subQ2=makeQuery(id+"F30.imprint","INTERSECT",VERTEX,{"disambiguationData":[OD(0.0)],"derivedFrom":[subQ1,subQ0]});Q3=makeQuery(id+"F30.imprint","IMPRINT",FACE,{"disambiguationData":[TD([[makeQuery(id+"F30.imprint","IMPRINT",EDGE,{"disambiguationData":[TD([[subQ2,-1.0]])],"derivedFrom":subQ1}),1.0]])]});}
            var Q4;
            {var subQ0=sQuery(id+"F30.wireOp",EDGE,"E66.1");var subQ1=sQuery(id+"F30.wireOp",EDGE,"E65.bottom");var subQ2=makeQuery(id+"F30.imprint","INTERSECT",VERTEX,{"disambiguationData":[OD(0.0)],"derivedFrom":[subQ1,subQ0]});Q4=makeQuery(id+"F30.imprint","IMPRINT",FACE,{"disambiguationData":[TD([[makeQuery(id+"F30.imprint","IMPRINT",EDGE,{"disambiguationData":[TD([[subQ2,-1.0]])],"derivedFrom":subQ1}),-1.0]])]});}
            var Q5;
            {var subQ0=sQuery(id+"F30.wireOp",EDGE,"E66.1");var subQ1=sQuery(id+"F30.wireOp",EDGE,"E65.left");var subQ2=makeQuery(id+"F30.imprint","INTERSECT",VERTEX,{"disambiguationData":[OD(0.0)],"derivedFrom":[subQ1,subQ0]});Q5=makeQuery(id+"F30.imprint","IMPRINT",FACE,{"disambiguationData":[TD([[makeQuery(id+"F30.imprint","IMPRINT",EDGE,{"disambiguationData":[TD([[subQ2,-1.0]])],"derivedFrom":subQ1}),1.0]])]});}
            var Q6;
            {var subQ0=sQuery(id+"F30.wireOp",EDGE,"E66.1");var subQ1=sQuery(id+"F30.wireOp",EDGE,"E65.right");var subQ2=makeQuery(id+"F30.imprint","INTERSECT",VERTEX,{"disambiguationData":[OD(0.0)],"derivedFrom":[subQ1,subQ0]});Q6=makeQuery(id+"F30.imprint","IMPRINT",FACE,{"disambiguationData":[TD([[makeQuery(id+"F30.imprint","IMPRINT",EDGE,{"disambiguationData":[TD([[subQ2,-1.0]])],"derivedFrom":subQ1}),-1.0]])]});}
            var Q7;
            {var subQ0=sQuery(id+"F30.wireOp",EDGE,"E66.1");var subQ1=sQuery(id+"F30.wireOp",EDGE,"E65.top");var subQ2=makeQuery(id+"F30.imprint","INTERSECT",VERTEX,{"disambiguationData":[OD(0.0)],"derivedFrom":[subQ1,subQ0]});Q7=makeQuery(id+"F30.imprint","IMPRINT",FACE,{"disambiguationData":[TD([[makeQuery(id+"F30.imprint","IMPRINT",EDGE,{"disambiguationData":[TD([[subQ2,-1.0]])],"derivedFrom":subQ1}),1.0]])]});}
            extrude(context, id + "F31", {"entities" : qUnion([Q0, Q1, Q2, Q3, Q4, Q5, Q6, Q7]), "operationType" : NewBodyOperationType.ADD, "depth" : 3.86 * mm, "offsetDistance" : 25.4 * mm});
        }
        {
            var Q0;
            Q0=makeQuery(id+"F27.boolean.opBoolean","COPY",FACE,{"derivedFrom":makeQuery(id+"F27.opExtrude","CAP_FACE",FACE,{"disambiguationData":[OSD([sQuery(id+"F26.wireOp",EDGE,"E59.0")])],"isStart":false})});
            var sketch = newSketch(context, id + "F32", { "sketchPlane" : qUnion([Q0])});
            skLineSegment(sketch, "E67.0.0", {"start": v(-1.17, 9.14) * mm, "end": v(-3.48, 9.14) * mm});
            skArc(sketch, "E67.0.1", {"start": v(-3.48, 9.14) * mm, "mid": v(-2.33, 9.42) * mm, "end": v(-1.17, 9.14) * mm});
            skLineSegment(sketch, "E67.1.0", {"start": v(-4.58, 8.05) * mm, "end": v(-4.58, 5.74) * mm});
            skArc(sketch, "E67.1.1", {"start": v(-4.58, 5.74) * mm, "mid": v(-4.86, 6.9) * mm, "end": v(-4.58, 8.05) * mm});
            skLineSegment(sketch, "E67.2.0", {"start": v(-3.48, 4.65) * mm, "end": v(-1.17, 4.65) * mm});
            skArc(sketch, "E67.2.1", {"start": v(-1.17, 4.65) * mm, "mid": v(-2.33, 4.37) * mm, "end": v(-3.48, 4.65) * mm});
            skLineSegment(sketch, "E67.3.0", {"start": v(-0.08, 5.74) * mm, "end": v(-0.08, 8.05) * mm});
            skArc(sketch, "E67.3.1", {"start": v(-0.08, 8.05) * mm, "mid": v(0.2, 6.9) * mm, "end": v(-0.08, 5.74) * mm});
            skLineSegment(sketch, "E67.4.0", {"start": v(12.7, 9.14) * mm, "end": v(10.4, 9.14) * mm});
            skArc(sketch, "E67.4.1", {"start": v(10.4, 9.14) * mm, "mid": v(11.55, 9.42) * mm, "end": v(12.7, 9.14) * mm});
            skArc(sketch, "E67.5.0", {"start": v(9.3, 5.74) * mm, "mid": v(9.03, 6.9) * mm, "end": v(9.3, 8.05) * mm});
            skLineSegment(sketch, "E67.5.1", {"start": v(9.3, 8.05) * mm, "end": v(9.3, 5.74) * mm});
            skArc(sketch, "E67.6.0", {"start": v(12.7, 4.65) * mm, "mid": v(11.55, 4.37) * mm, "end": v(10.4, 4.65) * mm});
            skLineSegment(sketch, "E67.6.1", {"start": v(10.4, 4.65) * mm, "end": v(12.7, 4.65) * mm});
            skLineSegment(sketch, "E67.7.0", {"start": v(13.8, 5.74) * mm, "end": v(13.8, 8.05) * mm});
            skArc(sketch, "E67.7.1", {"start": v(13.8, 8.05) * mm, "mid": v(14.08, 6.9) * mm, "end": v(13.8, 5.74) * mm});
            skSolve(sketch);
        }
        {
            var Q0;
            Q0=qSketchRegion(id+"F32",true);
            extrude(context, id + "F33", {"entities" : qUnion([Q0]), "operationType" : NewBodyOperationType.ADD, "depth" : 3.86 * mm, "offsetDistance" : 25.4 * mm});
        }
        {
            var Q0;
            Q0=makeQuery(id+"F9.boolean.opBoolean","MERGE",FACE,{"derivedFrom":[makeQuery(id+"F1.opExtrude","CAP_FACE",FACE,{"disambiguationData":[OSD([sQuery(id+"F0.wireOp",EDGE,"E0.bottom"),sQuery(id+"F0.wireOp",EDGE,"E0.top"),sQuery(id+"F0.wireOp",EDGE,"E0.left"),sQuery(id+"F0.wireOp",EDGE,"E0.right")])],"isStart":false}),makeQuery(id+"F9.opExtrude","CAP_FACE",FACE,{"disambiguationData":[OSD([sQuery(id+"F8.wireOp",EDGE,"E8")])],"isStart":false})]});
            var sketch = newSketch(context, id + "F34", { "sketchPlane" : qUnion([Q0])});
            skLineSegment(sketch, "E68", {"start": v(-12.61, -18.5) * mm, "end": v(15.28, 9.27) * mm, "construction": true});
            skLineSegment(sketch, "E69", {"start": v(-5.58, -14.76) * mm, "end": v(-8.75, -11.58) * mm});
            skLineSegment(sketch, "E70", {"start": v(-8.75, -11.58) * mm, "end": v(-5.57, -8.4) * mm});
            skLineSegment(sketch, "E71", {"start": v(-5.57, -8.4) * mm, "end": v(-2.4, -11.6) * mm});
            skLineSegment(sketch, "E72", {"start": v(-2.4, -11.6) * mm, "end": v(-5.58, -14.76) * mm});
            skLineSegment(sketch, "E73", {"start": v(-7.16, -10) * mm, "end": v(-3.99, -13.18) * mm});
            skPoint(sketch, "E74", {"position": v(-5.57, -11.58) * mm});
            skLineSegment(sketch, "E75.1.0", {"start": v(11.49, -11.53) * mm, "end": v(8.3, -14.7) * mm});
            skLineSegment(sketch, "E75.1.1", {"start": v(8.31, -8.34) * mm, "end": v(11.49, -11.53) * mm});
            skLineSegment(sketch, "E75.1.2", {"start": v(5.13, -11.51) * mm, "end": v(8.31, -8.34) * mm});
            skLineSegment(sketch, "E75.1.3", {"start": v(8.3, -14.7) * mm, "end": v(5.13, -11.51) * mm});
            skLineSegment(sketch, "E75.2.0", {"start": v(8.25, 5.54) * mm, "end": v(11.42, 2.35) * mm});
            skLineSegment(sketch, "E75.2.1", {"start": v(5.06, 2.37) * mm, "end": v(8.25, 5.54) * mm});
            skLineSegment(sketch, "E75.2.2", {"start": v(8.24, -0.82) * mm, "end": v(5.06, 2.37) * mm});
            skLineSegment(sketch, "E75.2.3", {"start": v(11.42, 2.35) * mm, "end": v(8.24, -0.82) * mm});
            skLineSegment(sketch, "E75.3.0", {"start": v(-8.82, 2.3) * mm, "end": v(-5.63, 5.48) * mm});
            skLineSegment(sketch, "E75.3.1", {"start": v(-5.65, -0.88) * mm, "end": v(-8.82, 2.3) * mm});
            skLineSegment(sketch, "E75.3.2", {"start": v(-2.46, 2.29) * mm, "end": v(-5.65, -0.88) * mm});
            skLineSegment(sketch, "E75.3.3", {"start": v(-5.63, 5.48) * mm, "end": v(-2.46, 2.29) * mm});
            skPoint(sketch, "E75.center", {"position": v(1.33, -4.61) * mm});
            skCircle(sketch, "E76.0", {"center": v(-5.57, -11.58) * mm, "radius": 2.53 * mm});
            skCircle(sketch, "E77.1.0", {"center": v(8.3, -11.52) * mm, "radius": 2.53 * mm});
            skCircle(sketch, "E77.2.0", {"center": v(8.24, 2.36) * mm, "radius": 2.53 * mm});
            skCircle(sketch, "E77.3.0", {"center": v(-5.64, 2.3) * mm, "radius": 2.53 * mm});
            skSolve(sketch);
        }
        {
            var Q0;
            {var subQ0=sQuery(id+"F34.wireOp",EDGE,"E77.1.0");var subQ1=sQuery(id+"F34.wireOp",EDGE,"E75.1.0");var subQ2=makeQuery(id+"F34.imprint","INTERSECT",VERTEX,{"disambiguationData":[OD(0.0)],"derivedFrom":[subQ1,subQ0]});Q0=makeQuery(id+"F34.imprint","IMPRINT",FACE,{"disambiguationData":[TD([[makeQuery(id+"F34.imprint","IMPRINT",EDGE,{"disambiguationData":[TD([[subQ2,-1.0]])],"derivedFrom":subQ1}),1.0]])]});}
            var Q1;
            {var subQ0=sQuery(id+"F34.wireOp",EDGE,"E77.1.0");var subQ1=sQuery(id+"F34.wireOp",EDGE,"E75.1.3");var subQ2=makeQuery(id+"F34.imprint","INTERSECT",VERTEX,{"disambiguationData":[OD(0.0)],"derivedFrom":[subQ1,subQ0]});Q1=makeQuery(id+"F34.imprint","IMPRINT",FACE,{"disambiguationData":[TD([[makeQuery(id+"F34.imprint","IMPRINT",EDGE,{"disambiguationData":[TD([[subQ2,-1.0]])],"derivedFrom":subQ1}),1.0]])]});}
            var Q2;
            {var subQ0=sQuery(id+"F34.wireOp",EDGE,"E77.1.0");var subQ1=sQuery(id+"F34.wireOp",EDGE,"E75.1.1");var subQ2=makeQuery(id+"F34.imprint","INTERSECT",VERTEX,{"disambiguationData":[OD(0.0)],"derivedFrom":[subQ1,subQ0]});Q2=makeQuery(id+"F34.imprint","IMPRINT",FACE,{"disambiguationData":[TD([[makeQuery(id+"F34.imprint","IMPRINT",EDGE,{"disambiguationData":[TD([[subQ2,-1.0]])],"derivedFrom":subQ1}),1.0]])]});}
            var Q3;
            {var subQ0=sQuery(id+"F34.wireOp",EDGE,"E77.1.0");var subQ1=sQuery(id+"F34.wireOp",EDGE,"E75.1.2");var subQ2=makeQuery(id+"F34.imprint","INTERSECT",VERTEX,{"disambiguationData":[OD(0.0)],"derivedFrom":[subQ1,subQ0]});Q3=makeQuery(id+"F34.imprint","IMPRINT",FACE,{"disambiguationData":[TD([[makeQuery(id+"F34.imprint","IMPRINT",EDGE,{"disambiguationData":[TD([[subQ2,-1.0]])],"derivedFrom":subQ1}),1.0]])]});}
            var Q4;
            {var subQ0=sQuery(id+"F34.wireOp",EDGE,"E70");var subQ1=makeQuery(id+"F34.imprint","INTERSECT",VERTEX,{"derivedFrom":[subQ0,sQuery(id+"F34.wireOp",EDGE,"E73")]});Q4=makeQuery(id+"F34.imprint","IMPRINT",FACE,{"disambiguationData":[TD([[makeQuery(id+"F34.imprint","IMPRINT",EDGE,{"disambiguationData":[TD([[subQ1,1.0]])],"derivedFrom":subQ0}),1.0]])]});}
            var Q5;
            {var subQ0=sQuery(id+"F34.wireOp",EDGE,"E76.0");var subQ1=sQuery(id+"F34.wireOp",EDGE,"E71");var subQ2=makeQuery(id+"F34.imprint","INTERSECT",VERTEX,{"disambiguationData":[OD(0.0)],"derivedFrom":[subQ1,subQ0]});Q5=makeQuery(id+"F34.imprint","IMPRINT",FACE,{"disambiguationData":[TD([[makeQuery(id+"F34.imprint","IMPRINT",EDGE,{"disambiguationData":[TD([[subQ2,-1.0]])],"derivedFrom":subQ1}),1.0]])]});}
            var Q6;
            {var subQ0=sQuery(id+"F34.wireOp",EDGE,"E72");var subQ1=makeQuery(id+"F34.imprint","INTERSECT",VERTEX,{"derivedFrom":[subQ0,sQuery(id+"F34.wireOp",EDGE,"E73")]});Q6=makeQuery(id+"F34.imprint","IMPRINT",FACE,{"disambiguationData":[TD([[makeQuery(id+"F34.imprint","IMPRINT",EDGE,{"disambiguationData":[TD([[subQ1,1.0]])],"derivedFrom":subQ0}),1.0]])]});}
            var Q7;
            {var subQ0=sQuery(id+"F34.wireOp",EDGE,"E76.0");var subQ1=sQuery(id+"F34.wireOp",EDGE,"E69");var subQ2=makeQuery(id+"F34.imprint","INTERSECT",VERTEX,{"disambiguationData":[OD(0.0)],"derivedFrom":[subQ1,subQ0]});Q7=makeQuery(id+"F34.imprint","IMPRINT",FACE,{"disambiguationData":[TD([[makeQuery(id+"F34.imprint","IMPRINT",EDGE,{"disambiguationData":[TD([[subQ2,-1.0]])],"derivedFrom":subQ1}),1.0]])]});}
            var Q8;
            {var subQ0=sQuery(id+"F34.wireOp",EDGE,"E77.3.0");var subQ1=sQuery(id+"F34.wireOp",EDGE,"E75.3.0");var subQ2=makeQuery(id+"F34.imprint","INTERSECT",VERTEX,{"disambiguationData":[OD(0.0)],"derivedFrom":[subQ1,subQ0]});Q8=makeQuery(id+"F34.imprint","IMPRINT",FACE,{"disambiguationData":[TD([[makeQuery(id+"F34.imprint","IMPRINT",EDGE,{"disambiguationData":[TD([[subQ2,-1.0]])],"derivedFrom":subQ1}),1.0]])]});}
            var Q9;
            {var subQ0=sQuery(id+"F34.wireOp",EDGE,"E77.3.0");var subQ1=sQuery(id+"F34.wireOp",EDGE,"E75.3.3");var subQ2=makeQuery(id+"F34.imprint","INTERSECT",VERTEX,{"disambiguationData":[OD(0.0)],"derivedFrom":[subQ1,subQ0]});Q9=makeQuery(id+"F34.imprint","IMPRINT",FACE,{"disambiguationData":[TD([[makeQuery(id+"F34.imprint","IMPRINT",EDGE,{"disambiguationData":[TD([[subQ2,-1.0]])],"derivedFrom":subQ1}),1.0]])]});}
            var Q10;
            {var subQ0=sQuery(id+"F34.wireOp",EDGE,"E77.3.0");var subQ1=sQuery(id+"F34.wireOp",EDGE,"E75.3.1");var subQ2=makeQuery(id+"F34.imprint","INTERSECT",VERTEX,{"disambiguationData":[OD(0.0)],"derivedFrom":[subQ1,subQ0]});Q10=makeQuery(id+"F34.imprint","IMPRINT",FACE,{"disambiguationData":[TD([[makeQuery(id+"F34.imprint","IMPRINT",EDGE,{"disambiguationData":[TD([[subQ2,-1.0]])],"derivedFrom":subQ1}),1.0]])]});}
            var Q11;
            {var subQ0=sQuery(id+"F34.wireOp",EDGE,"E77.3.0");var subQ1=sQuery(id+"F34.wireOp",EDGE,"E75.3.2");var subQ2=makeQuery(id+"F34.imprint","INTERSECT",VERTEX,{"disambiguationData":[OD(0.0)],"derivedFrom":[subQ1,subQ0]});Q11=makeQuery(id+"F34.imprint","IMPRINT",FACE,{"disambiguationData":[TD([[makeQuery(id+"F34.imprint","IMPRINT",EDGE,{"disambiguationData":[TD([[subQ2,-1.0]])],"derivedFrom":subQ1}),1.0]])]});}
            var Q12;
            {var subQ0=sQuery(id+"F34.wireOp",EDGE,"E77.2.0");var subQ1=sQuery(id+"F34.wireOp",EDGE,"E75.2.0");var subQ2=makeQuery(id+"F34.imprint","INTERSECT",VERTEX,{"disambiguationData":[OD(0.0)],"derivedFrom":[subQ1,subQ0]});Q12=makeQuery(id+"F34.imprint","IMPRINT",FACE,{"disambiguationData":[TD([[makeQuery(id+"F34.imprint","IMPRINT",EDGE,{"disambiguationData":[TD([[subQ2,-1.0]])],"derivedFrom":subQ1}),1.0]])]});}
            var Q13;
            {var subQ0=sQuery(id+"F34.wireOp",EDGE,"E77.2.0");var subQ1=sQuery(id+"F34.wireOp",EDGE,"E75.2.1");var subQ2=makeQuery(id+"F34.imprint","INTERSECT",VERTEX,{"disambiguationData":[OD(0.0)],"derivedFrom":[subQ1,subQ0]});Q13=makeQuery(id+"F34.imprint","IMPRINT",FACE,{"disambiguationData":[TD([[makeQuery(id+"F34.imprint","IMPRINT",EDGE,{"disambiguationData":[TD([[subQ2,-1.0]])],"derivedFrom":subQ1}),1.0]])]});}
            var Q14;
            {var subQ0=sQuery(id+"F34.wireOp",EDGE,"E77.2.0");var subQ1=sQuery(id+"F34.wireOp",EDGE,"E75.2.2");var subQ2=makeQuery(id+"F34.imprint","INTERSECT",VERTEX,{"disambiguationData":[OD(0.0)],"derivedFrom":[subQ1,subQ0]});Q14=makeQuery(id+"F34.imprint","IMPRINT",FACE,{"disambiguationData":[TD([[makeQuery(id+"F34.imprint","IMPRINT",EDGE,{"disambiguationData":[TD([[subQ2,-1.0]])],"derivedFrom":subQ1}),1.0]])]});}
            var Q15;
            {var subQ0=sQuery(id+"F34.wireOp",EDGE,"E77.2.0");var subQ1=sQuery(id+"F34.wireOp",EDGE,"E75.2.3");var subQ2=makeQuery(id+"F34.imprint","INTERSECT",VERTEX,{"disambiguationData":[OD(0.0)],"derivedFrom":[subQ1,subQ0]});Q15=makeQuery(id+"F34.imprint","IMPRINT",FACE,{"disambiguationData":[TD([[makeQuery(id+"F34.imprint","IMPRINT",EDGE,{"disambiguationData":[TD([[subQ2,-1.0]])],"derivedFrom":subQ1}),1.0]])]});}
            extrude(context, id + "F35", {"entities" : qUnion([Q0, Q1, Q2, Q3, Q4, Q5, Q6, Q7, Q8, Q9, Q10, Q11, Q12, Q13, Q14, Q15]), "operationType" : NewBodyOperationType.ADD, "oppositeDirection" : true, "depth" : 13.8 * mm, "offsetDistance" : 25.4 * mm});
        }
        {
            var Q0;
            {var subQ0=sQuery(id+"F34.wireOp",EDGE,"E77.3.0");var subQ1=sQuery(id+"F34.wireOp",EDGE,"E77.2.0");var subQ2=sQuery(id+"F34.wireOp",EDGE,"E77.1.0");var subQ3=sQuery(id+"F34.wireOp",EDGE,"E76.0");Q0=makeQuery(id+"F35.boolean.opBoolean","MERGE",FACE,{"derivedFrom":[makeQuery(id+"F9.boolean.opBoolean","MERGE",FACE,{"derivedFrom":[makeQuery(id+"F1.opExtrude","CAP_FACE",FACE,{"disambiguationData":[OSD([sQuery(id+"F0.wireOp",EDGE,"E0.bottom"),sQuery(id+"F0.wireOp",EDGE,"E0.top"),sQuery(id+"F0.wireOp",EDGE,"E0.left"),sQuery(id+"F0.wireOp",EDGE,"E0.right")])],"isStart":false}),makeQuery(id+"F9.opExtrude","CAP_FACE",FACE,{"disambiguationData":[OSD([sQuery(id+"F8.wireOp",EDGE,"E8")])],"isStart":false})]}),makeQuery(id+"F35.opExtrude","CAP_FACE",FACE,{"disambiguationData":[OSD([sQuery(id+"F34.wireOp",EDGE,"E69"),subQ3])],"isStart":true}),makeQuery(id+"F35.opExtrude","CAP_FACE",FACE,{"disambiguationData":[OSD([sQuery(id+"F34.wireOp",EDGE,"E70"),subQ3])],"isStart":true}),makeQuery(id+"F35.opExtrude","CAP_FACE",FACE,{"disambiguationData":[OSD([sQuery(id+"F34.wireOp",EDGE,"E71"),subQ3])],"isStart":true}),makeQuery(id+"F35.opExtrude","CAP_FACE",FACE,{"disambiguationData":[OSD([sQuery(id+"F34.wireOp",EDGE,"E72"),subQ3])],"isStart":true}),makeQuery(id+"F35.opExtrude","CAP_FACE",FACE,{"disambiguationData":[OSD([sQuery(id+"F34.wireOp",EDGE,"E75.1.0"),subQ2])],"isStart":true}),makeQuery(id+"F35.opExtrude","CAP_FACE",FACE,{"disambiguationData":[OSD([sQuery(id+"F34.wireOp",EDGE,"E75.1.1"),subQ2])],"isStart":true}),makeQuery(id+"F35.opExtrude","CAP_FACE",FACE,{"disambiguationData":[OSD([sQuery(id+"F34.wireOp",EDGE,"E75.1.2"),subQ2])],"isStart":true}),makeQuery(id+"F35.opExtrude","CAP_FACE",FACE,{"disambiguationData":[OSD([sQuery(id+"F34.wireOp",EDGE,"E75.1.3"),subQ2])],"isStart":true}),makeQuery(id+"F35.opExtrude","CAP_FACE",FACE,{"disambiguationData":[OSD([sQuery(id+"F34.wireOp",EDGE,"E75.2.0"),subQ1])],"isStart":true}),makeQuery(id+"F35.opExtrude","CAP_FACE",FACE,{"disambiguationData":[OSD([sQuery(id+"F34.wireOp",EDGE,"E75.2.1"),subQ1])],"isStart":true}),makeQuery(id+"F35.opExtrude","CAP_FACE",FACE,{"disambiguationData":[OSD([sQuery(id+"F34.wireOp",EDGE,"E75.2.2"),subQ1])],"isStart":true}),makeQuery(id+"F35.opExtrude","CAP_FACE",FACE,{"disambiguationData":[OSD([sQuery(id+"F34.wireOp",EDGE,"E75.2.3"),subQ1])],"isStart":true}),makeQuery(id+"F35.opExtrude","CAP_FACE",FACE,{"disambiguationData":[OSD([sQuery(id+"F34.wireOp",EDGE,"E75.3.0"),subQ0])],"isStart":true}),makeQuery(id+"F35.opExtrude","CAP_FACE",FACE,{"disambiguationData":[OSD([sQuery(id+"F34.wireOp",EDGE,"E75.3.1"),subQ0])],"isStart":true}),makeQuery(id+"F35.opExtrude","CAP_FACE",FACE,{"disambiguationData":[OSD([sQuery(id+"F34.wireOp",EDGE,"E75.3.2"),subQ0])],"isStart":true}),makeQuery(id+"F35.opExtrude","CAP_FACE",FACE,{"disambiguationData":[OSD([sQuery(id+"F34.wireOp",EDGE,"E75.3.3"),subQ0])],"isStart":true})]});}
            var sketch = newSketch(context, id + "F36", { "sketchPlane" : qUnion([Q0])});
            skCircle(sketch, "E78", {"center": v(8.24, 2.36) * mm, "radius": 2.53 * mm});
            skLineSegment(sketch, "E79.0", {"start": v(10.65, 1.58) * mm, "end": v(9.01, -0.05) * mm});
            skLineSegment(sketch, "E79.1", {"start": v(9.02, 4.76) * mm, "end": v(10.65, 3.13) * mm});
            skLineSegment(sketch, "E79.2", {"start": v(5.84, 3.14) * mm, "end": v(7.48, 4.77) * mm});
            skLineSegment(sketch, "E79.3", {"start": v(7.46, -0.04) * mm, "end": v(5.84, 1.6) * mm});
            skCircle(sketch, "E80.1.0", {"center": v(-5.64, 2.3) * mm, "radius": 2.53 * mm});
            skLineSegment(sketch, "E80.1.1", {"start": v(-4.86, 4.7) * mm, "end": v(-3.23, 3.06) * mm});
            skLineSegment(sketch, "E80.1.2", {"start": v(-8.04, 3.07) * mm, "end": v(-6.4, 4.7) * mm});
            skLineSegment(sketch, "E80.1.3", {"start": v(-6.42, -0.1) * mm, "end": v(-8.05, 1.53) * mm});
            skLineSegment(sketch, "E80.1.4", {"start": v(-3.23, 1.52) * mm, "end": v(-4.87, -0.11) * mm});
            skCircle(sketch, "E80.2.0", {"center": v(-5.57, -11.58) * mm, "radius": 2.53 * mm});
            skLineSegment(sketch, "E80.2.1", {"start": v(-7.98, -10.8) * mm, "end": v(-6.34, -9.18) * mm});
            skLineSegment(sketch, "E80.2.2", {"start": v(-6.35, -13.99) * mm, "end": v(-7.98, -12.35) * mm});
            skLineSegment(sketch, "E80.2.3", {"start": v(-3.17, -12.36) * mm, "end": v(-4.8, -14) * mm});
            skLineSegment(sketch, "E80.2.4", {"start": v(-4.8, -9.18) * mm, "end": v(-3.17, -10.82) * mm});
            skCircle(sketch, "E80.3.0", {"center": v(8.3, -11.52) * mm, "radius": 2.53 * mm});
            skLineSegment(sketch, "E80.3.1", {"start": v(7.53, -13.93) * mm, "end": v(5.9, -12.29) * mm});
            skLineSegment(sketch, "E80.3.2", {"start": v(10.71, -12.3) * mm, "end": v(9.07, -13.93) * mm});
            skLineSegment(sketch, "E80.3.3", {"start": v(9.08, -9.12) * mm, "end": v(10.71, -10.75) * mm});
            skLineSegment(sketch, "E80.3.4", {"start": v(5.9, -10.74) * mm, "end": v(7.54, -9.11) * mm});
            skPoint(sketch, "E80.center", {"position": v(1.33, -4.61) * mm});
            skSolve(sketch);
        }
        {
            var Q0;
            {var subQ0=sQuery(id+"F36.wireOp",EDGE,"E79.1");var subQ1=sQuery(id+"F36.wireOp",EDGE,"E78");var subQ2=makeQuery(id+"F36.imprint","INTERSECT",VERTEX,{"disambiguationData":[OD(0.0)],"derivedFrom":[subQ1,subQ0]});Q0=makeQuery(id+"F36.imprint","IMPRINT",FACE,{"disambiguationData":[TD([[makeQuery(id+"F36.imprint","IMPRINT",EDGE,{"disambiguationData":[TD([[subQ2,1.0]])],"derivedFrom":subQ1}),1.0]])]});}
            var Q1;
            {var subQ0=sQuery(id+"F36.wireOp",EDGE,"E79.2");var subQ1=sQuery(id+"F36.wireOp",EDGE,"E78");var subQ2=makeQuery(id+"F36.imprint","INTERSECT",VERTEX,{"disambiguationData":[OD(0.0)],"derivedFrom":[subQ1,subQ0]});Q1=makeQuery(id+"F36.imprint","IMPRINT",FACE,{"disambiguationData":[TD([[makeQuery(id+"F36.imprint","IMPRINT",EDGE,{"disambiguationData":[TD([[subQ2,-1.0]])],"derivedFrom":subQ1}),1.0]])]});}
            var Q2;
            {var subQ0=sQuery(id+"F36.wireOp",EDGE,"E79.3");var subQ1=sQuery(id+"F36.wireOp",EDGE,"E78");var subQ2=makeQuery(id+"F36.imprint","INTERSECT",VERTEX,{"disambiguationData":[OD(0.0)],"derivedFrom":[subQ1,subQ0]});Q2=makeQuery(id+"F36.imprint","IMPRINT",FACE,{"disambiguationData":[TD([[makeQuery(id+"F36.imprint","IMPRINT",EDGE,{"disambiguationData":[TD([[subQ2,-1.0]])],"derivedFrom":subQ1}),1.0]])]});}
            var Q3;
            {var subQ0=sQuery(id+"F36.wireOp",EDGE,"E79.0");var subQ1=sQuery(id+"F36.wireOp",EDGE,"E78");var subQ2=makeQuery(id+"F36.imprint","INTERSECT",VERTEX,{"disambiguationData":[OD(0.0)],"derivedFrom":[subQ1,subQ0]});Q3=makeQuery(id+"F36.imprint","IMPRINT",FACE,{"disambiguationData":[TD([[makeQuery(id+"F36.imprint","IMPRINT",EDGE,{"disambiguationData":[TD([[subQ2,-1.0]])],"derivedFrom":subQ1}),1.0]])]});}
            var Q4;
            {var subQ0=sQuery(id+"F36.wireOp",EDGE,"E80.1.2");var subQ1=sQuery(id+"F36.wireOp",EDGE,"E80.1.0");var subQ2=makeQuery(id+"F36.imprint","INTERSECT",VERTEX,{"disambiguationData":[OD(0.0)],"derivedFrom":[subQ1,subQ0]});Q4=makeQuery(id+"F36.imprint","IMPRINT",FACE,{"disambiguationData":[TD([[makeQuery(id+"F36.imprint","IMPRINT",EDGE,{"disambiguationData":[TD([[subQ2,1.0]])],"derivedFrom":subQ1}),1.0]])]});}
            var Q5;
            {var subQ0=sQuery(id+"F36.wireOp",EDGE,"E80.1.3");var subQ1=sQuery(id+"F36.wireOp",EDGE,"E80.1.0");var subQ2=makeQuery(id+"F36.imprint","INTERSECT",VERTEX,{"disambiguationData":[OD(0.0)],"derivedFrom":[subQ1,subQ0]});Q5=makeQuery(id+"F36.imprint","IMPRINT",FACE,{"disambiguationData":[TD([[makeQuery(id+"F36.imprint","IMPRINT",EDGE,{"disambiguationData":[TD([[subQ2,-1.0]])],"derivedFrom":subQ1}),1.0]])]});}
            var Q6;
            {var subQ0=sQuery(id+"F36.wireOp",EDGE,"E80.1.4");var subQ1=sQuery(id+"F36.wireOp",EDGE,"E80.1.0");var subQ2=makeQuery(id+"F36.imprint","INTERSECT",VERTEX,{"disambiguationData":[OD(0.0)],"derivedFrom":[subQ1,subQ0]});Q6=makeQuery(id+"F36.imprint","IMPRINT",FACE,{"disambiguationData":[TD([[makeQuery(id+"F36.imprint","IMPRINT",EDGE,{"disambiguationData":[TD([[subQ2,-1.0]])],"derivedFrom":subQ1}),1.0]])]});}
            var Q7;
            {var subQ0=sQuery(id+"F36.wireOp",EDGE,"E80.1.1");var subQ1=sQuery(id+"F36.wireOp",EDGE,"E80.1.0");var subQ2=makeQuery(id+"F36.imprint","INTERSECT",VERTEX,{"disambiguationData":[OD(0.0)],"derivedFrom":[subQ1,subQ0]});Q7=makeQuery(id+"F36.imprint","IMPRINT",FACE,{"disambiguationData":[TD([[makeQuery(id+"F36.imprint","IMPRINT",EDGE,{"disambiguationData":[TD([[subQ2,-1.0]])],"derivedFrom":subQ1}),1.0]])]});}
            var Q8;
            {var subQ0=sQuery(id+"F36.wireOp",EDGE,"E80.2.2");var subQ1=sQuery(id+"F36.wireOp",EDGE,"E80.2.0");var subQ2=makeQuery(id+"F36.imprint","INTERSECT",VERTEX,{"disambiguationData":[OD(0.0)],"derivedFrom":[subQ1,subQ0]});Q8=makeQuery(id+"F36.imprint","IMPRINT",FACE,{"disambiguationData":[TD([[makeQuery(id+"F36.imprint","IMPRINT",EDGE,{"disambiguationData":[TD([[subQ2,1.0]])],"derivedFrom":subQ1}),1.0]])]});}
            var Q9;
            {var subQ0=sQuery(id+"F36.wireOp",EDGE,"E80.2.3");var subQ1=sQuery(id+"F36.wireOp",EDGE,"E80.2.0");var subQ2=makeQuery(id+"F36.imprint","INTERSECT",VERTEX,{"disambiguationData":[OD(0.0)],"derivedFrom":[subQ1,subQ0]});Q9=makeQuery(id+"F36.imprint","IMPRINT",FACE,{"disambiguationData":[TD([[makeQuery(id+"F36.imprint","IMPRINT",EDGE,{"disambiguationData":[TD([[subQ2,-1.0]])],"derivedFrom":subQ1}),1.0]])]});}
            var Q10;
            {var subQ0=sQuery(id+"F36.wireOp",EDGE,"E80.2.4");var subQ1=sQuery(id+"F36.wireOp",EDGE,"E80.2.0");var subQ2=makeQuery(id+"F36.imprint","INTERSECT",VERTEX,{"disambiguationData":[OD(0.0)],"derivedFrom":[subQ1,subQ0]});Q10=makeQuery(id+"F36.imprint","IMPRINT",FACE,{"disambiguationData":[TD([[makeQuery(id+"F36.imprint","IMPRINT",EDGE,{"disambiguationData":[TD([[subQ2,-1.0]])],"derivedFrom":subQ1}),1.0]])]});}
            var Q11;
            {var subQ0=sQuery(id+"F36.wireOp",EDGE,"E80.2.1");var subQ1=sQuery(id+"F36.wireOp",EDGE,"E80.2.0");var subQ2=makeQuery(id+"F36.imprint","INTERSECT",VERTEX,{"disambiguationData":[OD(0.0)],"derivedFrom":[subQ1,subQ0]});Q11=makeQuery(id+"F36.imprint","IMPRINT",FACE,{"disambiguationData":[TD([[makeQuery(id+"F36.imprint","IMPRINT",EDGE,{"disambiguationData":[TD([[subQ2,-1.0]])],"derivedFrom":subQ1}),1.0]])]});}
            var Q12;
            {var subQ0=sQuery(id+"F36.wireOp",EDGE,"E80.3.2");var subQ1=sQuery(id+"F36.wireOp",EDGE,"E80.3.0");var subQ2=makeQuery(id+"F36.imprint","INTERSECT",VERTEX,{"disambiguationData":[OD(0.0)],"derivedFrom":[subQ1,subQ0]});Q12=makeQuery(id+"F36.imprint","IMPRINT",FACE,{"disambiguationData":[TD([[makeQuery(id+"F36.imprint","IMPRINT",EDGE,{"disambiguationData":[TD([[subQ2,1.0]])],"derivedFrom":subQ1}),1.0]])]});}
            var Q13;
            {var subQ0=sQuery(id+"F36.wireOp",EDGE,"E80.3.3");var subQ1=sQuery(id+"F36.wireOp",EDGE,"E80.3.0");var subQ2=makeQuery(id+"F36.imprint","INTERSECT",VERTEX,{"disambiguationData":[OD(0.0)],"derivedFrom":[subQ1,subQ0]});Q13=makeQuery(id+"F36.imprint","IMPRINT",FACE,{"disambiguationData":[TD([[makeQuery(id+"F36.imprint","IMPRINT",EDGE,{"disambiguationData":[TD([[subQ2,-1.0]])],"derivedFrom":subQ1}),1.0]])]});}
            var Q14;
            {var subQ0=sQuery(id+"F36.wireOp",EDGE,"E80.3.4");var subQ1=sQuery(id+"F36.wireOp",EDGE,"E80.3.0");var subQ2=makeQuery(id+"F36.imprint","INTERSECT",VERTEX,{"disambiguationData":[OD(0.0)],"derivedFrom":[subQ1,subQ0]});Q14=makeQuery(id+"F36.imprint","IMPRINT",FACE,{"disambiguationData":[TD([[makeQuery(id+"F36.imprint","IMPRINT",EDGE,{"disambiguationData":[TD([[subQ2,-1.0]])],"derivedFrom":subQ1}),1.0]])]});}
            var Q15;
            {var subQ0=sQuery(id+"F36.wireOp",EDGE,"E80.3.1");var subQ1=sQuery(id+"F36.wireOp",EDGE,"E80.3.0");var subQ2=makeQuery(id+"F36.imprint","INTERSECT",VERTEX,{"disambiguationData":[OD(0.0)],"derivedFrom":[subQ1,subQ0]});Q15=makeQuery(id+"F36.imprint","IMPRINT",FACE,{"disambiguationData":[TD([[makeQuery(id+"F36.imprint","IMPRINT",EDGE,{"disambiguationData":[TD([[subQ2,-1.0]])],"derivedFrom":subQ1}),1.0]])]});}
            extrude(context, id + "F37", {"entities" : qUnion([Q0, Q1, Q2, Q3, Q4, Q5, Q6, Q7, Q8, Q9, Q10, Q11, Q12, Q13, Q14, Q15]), "operationType" : NewBodyOperationType.REMOVE, "oppositeDirection" : true, "depth" : 0.38 * mm, "offsetDistance" : 25.4 * mm});
        }
        {
            var Q0;
            {var subQ0=sQuery(id+"F34.wireOp",EDGE,"E77.3.0");var subQ1=sQuery(id+"F34.wireOp",EDGE,"E77.2.0");var subQ2=sQuery(id+"F34.wireOp",EDGE,"E77.1.0");var subQ3=sQuery(id+"F34.wireOp",EDGE,"E76.0");Q0=makeQuery(id+"F35.boolean.opBoolean","MERGE",FACE,{"derivedFrom":[makeQuery(id+"F7.boolean.opBoolean","MERGE",FACE,{"derivedFrom":[makeQuery(id+"F1.opExtrude","CAP_FACE",FACE,{"disambiguationData":[OSD([sQuery(id+"F0.wireOp",EDGE,"E0.bottom"),sQuery(id+"F0.wireOp",EDGE,"E0.top"),sQuery(id+"F0.wireOp",EDGE,"E0.left"),sQuery(id+"F0.wireOp",EDGE,"E0.right")])],"isStart":true}),makeQuery(id+"F7.opExtrude","CAP_FACE",FACE,{"disambiguationData":[OSD([sQuery(id+"F6.wireOp",EDGE,"E5")])],"isStart":false})]}),makeQuery(id+"F35.opExtrude","CAP_FACE",FACE,{"disambiguationData":[OSD([sQuery(id+"F34.wireOp",EDGE,"E69"),subQ3])],"isStart":false}),makeQuery(id+"F35.opExtrude","CAP_FACE",FACE,{"disambiguationData":[OSD([sQuery(id+"F34.wireOp",EDGE,"E70"),subQ3])],"isStart":false}),makeQuery(id+"F35.opExtrude","CAP_FACE",FACE,{"disambiguationData":[OSD([sQuery(id+"F34.wireOp",EDGE,"E71"),subQ3])],"isStart":false}),makeQuery(id+"F35.opExtrude","CAP_FACE",FACE,{"disambiguationData":[OSD([sQuery(id+"F34.wireOp",EDGE,"E72"),subQ3])],"isStart":false}),makeQuery(id+"F35.opExtrude","CAP_FACE",FACE,{"disambiguationData":[OSD([sQuery(id+"F34.wireOp",EDGE,"E75.1.0"),subQ2])],"isStart":false}),makeQuery(id+"F35.opExtrude","CAP_FACE",FACE,{"disambiguationData":[OSD([sQuery(id+"F34.wireOp",EDGE,"E75.1.1"),subQ2])],"isStart":false}),makeQuery(id+"F35.opExtrude","CAP_FACE",FACE,{"disambiguationData":[OSD([sQuery(id+"F34.wireOp",EDGE,"E75.1.2"),subQ2])],"isStart":false}),makeQuery(id+"F35.opExtrude","CAP_FACE",FACE,{"disambiguationData":[OSD([sQuery(id+"F34.wireOp",EDGE,"E75.1.3"),subQ2])],"isStart":false}),makeQuery(id+"F35.opExtrude","CAP_FACE",FACE,{"disambiguationData":[OSD([sQuery(id+"F34.wireOp",EDGE,"E75.2.0"),subQ1])],"isStart":false}),makeQuery(id+"F35.opExtrude","CAP_FACE",FACE,{"disambiguationData":[OSD([sQuery(id+"F34.wireOp",EDGE,"E75.2.1"),subQ1])],"isStart":false}),makeQuery(id+"F35.opExtrude","CAP_FACE",FACE,{"disambiguationData":[OSD([sQuery(id+"F34.wireOp",EDGE,"E75.2.2"),subQ1])],"isStart":false}),makeQuery(id+"F35.opExtrude","CAP_FACE",FACE,{"disambiguationData":[OSD([sQuery(id+"F34.wireOp",EDGE,"E75.2.3"),subQ1])],"isStart":false}),makeQuery(id+"F35.opExtrude","CAP_FACE",FACE,{"disambiguationData":[OSD([sQuery(id+"F34.wireOp",EDGE,"E75.3.0"),subQ0])],"isStart":false}),makeQuery(id+"F35.opExtrude","CAP_FACE",FACE,{"disambiguationData":[OSD([sQuery(id+"F34.wireOp",EDGE,"E75.3.1"),subQ0])],"isStart":false}),makeQuery(id+"F35.opExtrude","CAP_FACE",FACE,{"disambiguationData":[OSD([sQuery(id+"F34.wireOp",EDGE,"E75.3.2"),subQ0])],"isStart":false}),makeQuery(id+"F35.opExtrude","CAP_FACE",FACE,{"disambiguationData":[OSD([sQuery(id+"F34.wireOp",EDGE,"E75.3.3"),subQ0])],"isStart":false})]});}
            var sketch = newSketch(context, id + "F38", { "sketchPlane" : qUnion([Q0])});
            skCircle(sketch, "E81", {"center": v(8.24, -2.36) * mm, "radius": 2.53 * mm});
            skLineSegment(sketch, "E82.0", {"start": v(5.84, -3.14) * mm, "end": v(7.48, -4.77) * mm});
            skLineSegment(sketch, "E82.1", {"start": v(9.02, -4.76) * mm, "end": v(10.65, -3.13) * mm});
            skLineSegment(sketch, "E82.3", {"start": v(10.65, -1.58) * mm, "end": v(9.01, 0.05) * mm});
            skLineSegment(sketch, "E82.4", {"start": v(7.46, 0.04) * mm, "end": v(5.84, -1.6) * mm});
            skCircle(sketch, "E83.1.0", {"center": v(8.3, 11.52) * mm, "radius": 2.53 * mm});
            skLineSegment(sketch, "E83.1.1", {"start": v(5.9, 10.74) * mm, "end": v(7.54, 9.11) * mm});
            skLineSegment(sketch, "E83.1.2", {"start": v(9.08, 9.12) * mm, "end": v(10.71, 10.75) * mm});
            skLineSegment(sketch, "E83.1.3", {"start": v(10.71, 12.3) * mm, "end": v(9.07, 13.93) * mm});
            skLineSegment(sketch, "E83.1.4", {"start": v(7.53, 13.93) * mm, "end": v(5.9, 12.29) * mm});
            skCircle(sketch, "E83.2.0", {"center": v(-5.57, 11.58) * mm, "radius": 2.53 * mm});
            skLineSegment(sketch, "E83.2.1", {"start": v(-4.8, 9.18) * mm, "end": v(-3.17, 10.82) * mm});
            skLineSegment(sketch, "E83.2.2", {"start": v(-3.17, 12.36) * mm, "end": v(-4.8, 14) * mm});
            skLineSegment(sketch, "E83.2.3", {"start": v(-6.35, 13.99) * mm, "end": v(-7.98, 12.35) * mm});
            skLineSegment(sketch, "E83.2.4", {"start": v(-7.98, 10.8) * mm, "end": v(-6.34, 9.18) * mm});
            skCircle(sketch, "E83.3.0", {"center": v(-5.64, -2.3) * mm, "radius": 2.53 * mm});
            skLineSegment(sketch, "E83.3.1", {"start": v(-3.23, -1.52) * mm, "end": v(-4.87, 0.11) * mm});
            skLineSegment(sketch, "E83.3.2", {"start": v(-6.42, 0.1) * mm, "end": v(-8.05, -1.53) * mm});
            skLineSegment(sketch, "E83.3.3", {"start": v(-8.04, -3.07) * mm, "end": v(-6.4, -4.7) * mm});
            skLineSegment(sketch, "E83.3.4", {"start": v(-4.86, -4.7) * mm, "end": v(-3.23, -3.06) * mm});
            skPoint(sketch, "E83.center", {"position": v(1.33, 4.61) * mm});
            skSolve(sketch);
        }
        {
            var Q0;
            {var subQ0=sQuery(id+"F38.wireOp",EDGE,"E82.3");Q0=makeQuery(id+"F38.imprint","IMPRINT",FACE,{"disambiguationData":[TD([[makeQuery(id+"F38.imprint","IMPRINT",EDGE,{"derivedFrom":subQ0}),-1.0]])]});}
            var Q1;
            {var subQ0=sQuery(id+"F38.wireOp",EDGE,"E82.4");Q1=makeQuery(id+"F38.imprint","IMPRINT",FACE,{"disambiguationData":[TD([[makeQuery(id+"F38.imprint","IMPRINT",EDGE,{"derivedFrom":subQ0}),-1.0]])]});}
            var Q2;
            {var subQ0=sQuery(id+"F38.wireOp",EDGE,"E82.0");Q2=makeQuery(id+"F38.imprint","IMPRINT",FACE,{"disambiguationData":[TD([[makeQuery(id+"F38.imprint","IMPRINT",EDGE,{"derivedFrom":subQ0}),-1.0]])]});}
            var Q3;
            {var subQ0=sQuery(id+"F38.wireOp",EDGE,"E82.1");Q3=makeQuery(id+"F38.imprint","IMPRINT",FACE,{"disambiguationData":[TD([[makeQuery(id+"F38.imprint","IMPRINT",EDGE,{"derivedFrom":subQ0}),-1.0]])]});}
            var Q4;
            {var subQ0=sQuery(id+"F38.wireOp",EDGE,"E83.1.4");Q4=makeQuery(id+"F38.imprint","IMPRINT",FACE,{"disambiguationData":[TD([[makeQuery(id+"F38.imprint","IMPRINT",EDGE,{"derivedFrom":subQ0}),-1.0]])]});}
            var Q5;
            {var subQ0=sQuery(id+"F38.wireOp",EDGE,"E83.1.1");Q5=makeQuery(id+"F38.imprint","IMPRINT",FACE,{"disambiguationData":[TD([[makeQuery(id+"F38.imprint","IMPRINT",EDGE,{"derivedFrom":subQ0}),-1.0]])]});}
            var Q6;
            {var subQ0=sQuery(id+"F38.wireOp",EDGE,"E83.1.2");Q6=makeQuery(id+"F38.imprint","IMPRINT",FACE,{"disambiguationData":[TD([[makeQuery(id+"F38.imprint","IMPRINT",EDGE,{"derivedFrom":subQ0}),-1.0]])]});}
            var Q7;
            {var subQ0=sQuery(id+"F38.wireOp",EDGE,"E83.1.3");Q7=makeQuery(id+"F38.imprint","IMPRINT",FACE,{"disambiguationData":[TD([[makeQuery(id+"F38.imprint","IMPRINT",EDGE,{"derivedFrom":subQ0}),-1.0]])]});}
            var Q8;
            {var subQ0=sQuery(id+"F38.wireOp",EDGE,"E83.2.4");Q8=makeQuery(id+"F38.imprint","IMPRINT",FACE,{"disambiguationData":[TD([[makeQuery(id+"F38.imprint","IMPRINT",EDGE,{"derivedFrom":subQ0}),-1.0]])]});}
            var Q9;
            {var subQ0=sQuery(id+"F38.wireOp",EDGE,"E83.2.1");Q9=makeQuery(id+"F38.imprint","IMPRINT",FACE,{"disambiguationData":[TD([[makeQuery(id+"F38.imprint","IMPRINT",EDGE,{"derivedFrom":subQ0}),-1.0]])]});}
            var Q10;
            {var subQ0=sQuery(id+"F38.wireOp",EDGE,"E83.2.2");Q10=makeQuery(id+"F38.imprint","IMPRINT",FACE,{"disambiguationData":[TD([[makeQuery(id+"F38.imprint","IMPRINT",EDGE,{"derivedFrom":subQ0}),-1.0]])]});}
            var Q11;
            {var subQ0=sQuery(id+"F38.wireOp",EDGE,"E83.2.3");Q11=makeQuery(id+"F38.imprint","IMPRINT",FACE,{"disambiguationData":[TD([[makeQuery(id+"F38.imprint","IMPRINT",EDGE,{"derivedFrom":subQ0}),-1.0]])]});}
            var Q12;
            {var subQ0=sQuery(id+"F38.wireOp",EDGE,"E83.3.4");Q12=makeQuery(id+"F38.imprint","IMPRINT",FACE,{"disambiguationData":[TD([[makeQuery(id+"F38.imprint","IMPRINT",EDGE,{"derivedFrom":subQ0}),-1.0]])]});}
            var Q13;
            {var subQ0=sQuery(id+"F38.wireOp",EDGE,"E83.3.1");Q13=makeQuery(id+"F38.imprint","IMPRINT",FACE,{"disambiguationData":[TD([[makeQuery(id+"F38.imprint","IMPRINT",EDGE,{"derivedFrom":subQ0}),-1.0]])]});}
            var Q14;
            {var subQ0=sQuery(id+"F38.wireOp",EDGE,"E83.3.2");Q14=makeQuery(id+"F38.imprint","IMPRINT",FACE,{"disambiguationData":[TD([[makeQuery(id+"F38.imprint","IMPRINT",EDGE,{"derivedFrom":subQ0}),-1.0]])]});}
            var Q15;
            {var subQ0=sQuery(id+"F38.wireOp",EDGE,"E83.3.3");Q15=makeQuery(id+"F38.imprint","IMPRINT",FACE,{"disambiguationData":[TD([[makeQuery(id+"F38.imprint","IMPRINT",EDGE,{"derivedFrom":subQ0}),-1.0]])]});}
            extrude(context, id + "F39", {"entities" : qUnion([Q0, Q1, Q2, Q3, Q4, Q5, Q6, Q7, Q8, Q9, Q10, Q11, Q12, Q13, Q14, Q15]), "operationType" : NewBodyOperationType.REMOVE, "oppositeDirection" : true, "depth" : 0.38 * mm, "offsetDistance" : 25.4 * mm});
        }
        {
            var Q0;
            {var subQ0=sQuery(id+"F34.wireOp",EDGE,"E77.3.0");var subQ1=sQuery(id+"F34.wireOp",EDGE,"E77.2.0");var subQ2=sQuery(id+"F34.wireOp",EDGE,"E77.1.0");var subQ3=sQuery(id+"F34.wireOp",EDGE,"E76.0");Q0=makeQuery(id+"F35.boolean.opBoolean","MERGE",FACE,{"derivedFrom":[makeQuery(id+"F9.boolean.opBoolean","MERGE",FACE,{"derivedFrom":[makeQuery(id+"F1.opExtrude","CAP_FACE",FACE,{"disambiguationData":[OSD([sQuery(id+"F0.wireOp",EDGE,"E0.bottom"),sQuery(id+"F0.wireOp",EDGE,"E0.top"),sQuery(id+"F0.wireOp",EDGE,"E0.left"),sQuery(id+"F0.wireOp",EDGE,"E0.right")])],"isStart":false}),makeQuery(id+"F9.opExtrude","CAP_FACE",FACE,{"disambiguationData":[OSD([sQuery(id+"F8.wireOp",EDGE,"E8")])],"isStart":false})]}),makeQuery(id+"F35.opExtrude","CAP_FACE",FACE,{"disambiguationData":[OSD([sQuery(id+"F34.wireOp",EDGE,"E69"),subQ3])],"isStart":true}),makeQuery(id+"F35.opExtrude","CAP_FACE",FACE,{"disambiguationData":[OSD([sQuery(id+"F34.wireOp",EDGE,"E70"),subQ3])],"isStart":true}),makeQuery(id+"F35.opExtrude","CAP_FACE",FACE,{"disambiguationData":[OSD([sQuery(id+"F34.wireOp",EDGE,"E71"),subQ3])],"isStart":true}),makeQuery(id+"F35.opExtrude","CAP_FACE",FACE,{"disambiguationData":[OSD([sQuery(id+"F34.wireOp",EDGE,"E72"),subQ3])],"isStart":true}),makeQuery(id+"F35.opExtrude","CAP_FACE",FACE,{"disambiguationData":[OSD([sQuery(id+"F34.wireOp",EDGE,"E75.1.0"),subQ2])],"isStart":true}),makeQuery(id+"F35.opExtrude","CAP_FACE",FACE,{"disambiguationData":[OSD([sQuery(id+"F34.wireOp",EDGE,"E75.1.1"),subQ2])],"isStart":true}),makeQuery(id+"F35.opExtrude","CAP_FACE",FACE,{"disambiguationData":[OSD([sQuery(id+"F34.wireOp",EDGE,"E75.1.2"),subQ2])],"isStart":true}),makeQuery(id+"F35.opExtrude","CAP_FACE",FACE,{"disambiguationData":[OSD([sQuery(id+"F34.wireOp",EDGE,"E75.1.3"),subQ2])],"isStart":true}),makeQuery(id+"F35.opExtrude","CAP_FACE",FACE,{"disambiguationData":[OSD([sQuery(id+"F34.wireOp",EDGE,"E75.2.0"),subQ1])],"isStart":true}),makeQuery(id+"F35.opExtrude","CAP_FACE",FACE,{"disambiguationData":[OSD([sQuery(id+"F34.wireOp",EDGE,"E75.2.1"),subQ1])],"isStart":true}),makeQuery(id+"F35.opExtrude","CAP_FACE",FACE,{"disambiguationData":[OSD([sQuery(id+"F34.wireOp",EDGE,"E75.2.2"),subQ1])],"isStart":true}),makeQuery(id+"F35.opExtrude","CAP_FACE",FACE,{"disambiguationData":[OSD([sQuery(id+"F34.wireOp",EDGE,"E75.2.3"),subQ1])],"isStart":true}),makeQuery(id+"F35.opExtrude","CAP_FACE",FACE,{"disambiguationData":[OSD([sQuery(id+"F34.wireOp",EDGE,"E75.3.0"),subQ0])],"isStart":true}),makeQuery(id+"F35.opExtrude","CAP_FACE",FACE,{"disambiguationData":[OSD([sQuery(id+"F34.wireOp",EDGE,"E75.3.1"),subQ0])],"isStart":true}),makeQuery(id+"F35.opExtrude","CAP_FACE",FACE,{"disambiguationData":[OSD([sQuery(id+"F34.wireOp",EDGE,"E75.3.2"),subQ0])],"isStart":true}),makeQuery(id+"F35.opExtrude","CAP_FACE",FACE,{"disambiguationData":[OSD([sQuery(id+"F34.wireOp",EDGE,"E75.3.3"),subQ0])],"isStart":true})]});}
            extrude(context, id + "F40", {"entities" : qUnion([Q0]), "operationType" : NewBodyOperationType.ADD, "depth" : 12.2 * mm, "offsetDistance" : 25 * mm});
        }
        {
            var Q0;
            {var subQ0=sQuery(id+"F0.wireOp",EDGE,"E0.left");Q0=makeQuery(id+"F40.boolean.opBoolean","MERGE",FACE,{"derivedFrom":[makeQuery(id+"F1.opExtrude","SWEPT_FACE",FACE,{"disambiguationData":[OSD([subQ0])]}),makeQuery(id+"F40.opExtrude","SWEPT_FACE",FACE,{"disambiguationData":[OSD([subQ0])]})]});}
            var sketch = newSketch(context, id + "F41", { "sketchPlane" : qUnion([Q0])});
            skCircle(sketch, "E84.0", {"center": v(-2.33, 6.9) * mm, "radius": 2.53 * mm});
            skLineSegment(sketch, "E84.1", {"start": v(-4.58, 8.05) * mm, "end": v(-4.58, 5.74) * mm});
            skLineSegment(sketch, "E84.2", {"start": v(-3.48, 4.65) * mm, "end": v(-1.17, 4.65) * mm});
            skLineSegment(sketch, "E84.3", {"start": v(-1.17, 9.14) * mm, "end": v(-3.48, 9.14) * mm});
            skLineSegment(sketch, "E84.4", {"start": v(-0.08, 5.74) * mm, "end": v(-0.08, 8.05) * mm});
            skPoint(sketch, "E85", {"position": v(11.55, 6.9) * mm});
            skLineSegment(sketch, "E86.0.1.0", {"start": v(-4.58, 20.25) * mm, "end": v(-4.58, 17.94) * mm});
            skCircle(sketch, "E86.0.1.1", {"center": v(-2.33, 19.1) * mm, "radius": 2.53 * mm});
            skLineSegment(sketch, "E86.0.1.2", {"start": v(-1.17, 21.34) * mm, "end": v(-3.48, 21.34) * mm});
            skLineSegment(sketch, "E86.0.1.3", {"start": v(-0.08, 17.94) * mm, "end": v(-0.08, 20.25) * mm});
            skLineSegment(sketch, "E86.0.1.4", {"start": v(-3.48, 16.85) * mm, "end": v(-1.17, 16.85) * mm});
            skLineSegment(sketch, "E86.1.0.0", {"start": v(9.3, 8.05) * mm, "end": v(9.3, 5.74) * mm});
            skCircle(sketch, "E86.1.0.1", {"center": v(11.55, 6.9) * mm, "radius": 2.53 * mm});
            skLineSegment(sketch, "E86.1.0.2", {"start": v(12.7, 9.14) * mm, "end": v(10.4, 9.14) * mm});
            skLineSegment(sketch, "E86.1.0.3", {"start": v(13.8, 5.74) * mm, "end": v(13.8, 8.05) * mm});
            skLineSegment(sketch, "E86.1.0.4", {"start": v(10.4, 4.65) * mm, "end": v(12.7, 4.65) * mm});
            skLineSegment(sketch, "E86.1.1.0", {"start": v(9.3, 20.25) * mm, "end": v(9.3, 17.94) * mm});
            skCircle(sketch, "E86.1.1.1", {"center": v(11.55, 19.1) * mm, "radius": 2.53 * mm});
            skLineSegment(sketch, "E86.1.1.2", {"start": v(12.7, 21.34) * mm, "end": v(10.4, 21.34) * mm});
            skLineSegment(sketch, "E86.1.1.3", {"start": v(13.8, 17.94) * mm, "end": v(13.8, 20.25) * mm});
            skLineSegment(sketch, "E86.1.1.4", {"start": v(10.4, 16.85) * mm, "end": v(12.7, 16.85) * mm});
            skLineSegment(sketch, "E86.direction1", {"start": v(-4.58, 5.74) * mm, "end": v(9.3, 5.74) * mm, "construction": true});
            skLineSegment(sketch, "E86.direction2", {"start": v(-4.58, 5.74) * mm, "end": v(-4.58, 17.94) * mm, "construction": true});
            skLineSegment(sketch, "E87", {"start": v(-9.27, 13) * mm, "end": v(18.5, 13) * mm, "construction": true});
            skLineSegment(sketch, "E88", {"start": v(-2.33, 19.1) * mm, "end": v(-2.33, 6.9) * mm, "construction": true});
            skPoint(sketch, "E89", {"position": v(-2.33, 13) * mm});
            skSolve(sketch);
        }
        {
            var Q0;
            {var subQ1=sQuery(id+"F41.wireOp",EDGE,"E86.1.1.0");Q0=makeQuery(id+"F41.imprint","IMPRINT",FACE,{"disambiguationData":[TD([[makeQuery(id+"F41.imprint","IMPRINT",EDGE,{"derivedFrom":subQ1}),1.0]])]});}
            var Q1;
            {var subQ1=sQuery(id+"F41.wireOp",EDGE,"E86.0.1.0");Q1=makeQuery(id+"F41.imprint","IMPRINT",FACE,{"disambiguationData":[TD([[makeQuery(id+"F41.imprint","IMPRINT",EDGE,{"derivedFrom":subQ1}),1.0]])]});}
            extrude(context, id + "F42", {"entities" : qUnion([Q0, Q1]), "operationType" : NewBodyOperationType.REMOVE, "oppositeDirection" : true, "depth" : 6.9 * mm, "offsetDistance" : 25 * mm});
        }
        {
            var Q0;
            {var subQ0=sQuery(id+"F41.wireOp",EDGE,"E86.1.1.4");Q0=makeQuery(id+"F41.imprint","IMPRINT",FACE,{"disambiguationData":[TD([[makeQuery(id+"F41.imprint","IMPRINT",EDGE,{"derivedFrom":subQ0}),-1.0]])]});}
            var Q1;
            {var subQ0=sQuery(id+"F41.wireOp",EDGE,"E86.1.1.3");Q1=makeQuery(id+"F41.imprint","IMPRINT",FACE,{"disambiguationData":[TD([[makeQuery(id+"F41.imprint","IMPRINT",EDGE,{"derivedFrom":subQ0}),-1.0]])]});}
            var Q2;
            {var subQ0=sQuery(id+"F41.wireOp",EDGE,"E86.1.1.0");Q2=makeQuery(id+"F41.imprint","IMPRINT",FACE,{"disambiguationData":[TD([[makeQuery(id+"F41.imprint","IMPRINT",EDGE,{"derivedFrom":subQ0}),-1.0]])]});}
            var Q3;
            {var subQ0=sQuery(id+"F41.wireOp",EDGE,"E86.1.1.2");Q3=makeQuery(id+"F41.imprint","IMPRINT",FACE,{"disambiguationData":[TD([[makeQuery(id+"F41.imprint","IMPRINT",EDGE,{"derivedFrom":subQ0}),-1.0]])]});}
            var Q4;
            {var subQ0=sQuery(id+"F41.wireOp",EDGE,"E86.0.1.4");Q4=makeQuery(id+"F41.imprint","IMPRINT",FACE,{"disambiguationData":[TD([[makeQuery(id+"F41.imprint","IMPRINT",EDGE,{"derivedFrom":subQ0}),-1.0]])]});}
            var Q5;
            {var subQ0=sQuery(id+"F41.wireOp",EDGE,"E86.0.1.3");Q5=makeQuery(id+"F41.imprint","IMPRINT",FACE,{"disambiguationData":[TD([[makeQuery(id+"F41.imprint","IMPRINT",EDGE,{"derivedFrom":subQ0}),-1.0]])]});}
            var Q6;
            {var subQ0=sQuery(id+"F41.wireOp",EDGE,"E86.0.1.2");Q6=makeQuery(id+"F41.imprint","IMPRINT",FACE,{"disambiguationData":[TD([[makeQuery(id+"F41.imprint","IMPRINT",EDGE,{"derivedFrom":subQ0}),-1.0]])]});}
            var Q7;
            {var subQ0=sQuery(id+"F41.wireOp",EDGE,"E86.0.1.0");Q7=makeQuery(id+"F41.imprint","IMPRINT",FACE,{"disambiguationData":[TD([[makeQuery(id+"F41.imprint","IMPRINT",EDGE,{"derivedFrom":subQ0}),-1.0]])]});}
            extrude(context, id + "F43", {"entities" : qUnion([Q0, Q1, Q2, Q3, Q4, Q5, Q6, Q7]), "operationType" : NewBodyOperationType.REMOVE, "oppositeDirection" : true, "depth" : 0.2 * mm, "offsetDistance" : 25 * mm});
        }
        {
            var Q0;
            {var subQ0=sQuery(id+"F0.wireOp",EDGE,"E0.right");Q0=makeQuery(id+"F40.boolean.opBoolean","MERGE",FACE,{"derivedFrom":[makeQuery(id+"F1.opExtrude","SWEPT_FACE",FACE,{"disambiguationData":[OSD([subQ0])]}),makeQuery(id+"F40.opExtrude","SWEPT_FACE",FACE,{"disambiguationData":[OSD([subQ0])]})]});}
            var sketch = newSketch(context, id + "F44", { "sketchPlane" : qUnion([Q0])});
            skCircle(sketch, "E90.0", {"center": v(-11.55, 19.1) * mm, "radius": 2.53 * mm});
            skLineSegment(sketch, "E90.1", {"start": v(-10.4, 16.85) * mm, "end": v(-12.7, 16.85) * mm});
            skLineSegment(sketch, "E90.2", {"start": v(-13.8, 17.94) * mm, "end": v(-13.8, 20.25) * mm});
            skLineSegment(sketch, "E90.3", {"start": v(-12.7, 21.34) * mm, "end": v(-10.4, 21.34) * mm});
            skLineSegment(sketch, "E90.4", {"start": v(-9.3, 20.25) * mm, "end": v(-9.3, 17.94) * mm});
            skCircle(sketch, "E90.5", {"center": v(2.33, 19.1) * mm, "radius": 2.53 * mm});
            skLineSegment(sketch, "E90.6", {"start": v(3.48, 16.85) * mm, "end": v(1.17, 16.85) * mm});
            skLineSegment(sketch, "E90.7", {"start": v(0.08, 17.94) * mm, "end": v(0.08, 20.25) * mm});
            skLineSegment(sketch, "E90.8", {"start": v(1.17, 21.34) * mm, "end": v(3.48, 21.34) * mm});
            skLineSegment(sketch, "E90.9", {"start": v(4.58, 20.25) * mm, "end": v(4.58, 17.94) * mm});
            skSolve(sketch);
        }
        {
            var Q0;
            {var subQ0=sQuery(id+"F44.wireOp",EDGE,"E90.1");Q0=makeQuery(id+"F44.imprint","IMPRINT",FACE,{"disambiguationData":[TD([[makeQuery(id+"F44.imprint","IMPRINT",EDGE,{"derivedFrom":subQ0}),-1.0]])]});}
            var Q1;
            {var subQ0=sQuery(id+"F44.wireOp",EDGE,"E90.6");Q1=makeQuery(id+"F44.imprint","IMPRINT",FACE,{"disambiguationData":[TD([[makeQuery(id+"F44.imprint","IMPRINT",EDGE,{"derivedFrom":subQ0}),-1.0]])]});}
            extrude(context, id + "F45", {"entities" : qUnion([Q0, Q1]), "operationType" : NewBodyOperationType.REMOVE, "oppositeDirection" : true, "depth" : 6.7 * mm, "offsetDistance" : 25 * mm});
        }
        {
            var Q0;
            {var subQ0=sQuery(id+"F44.wireOp",EDGE,"E90.3");Q0=makeQuery(id+"F44.imprint","IMPRINT",FACE,{"disambiguationData":[TD([[makeQuery(id+"F44.imprint","IMPRINT",EDGE,{"derivedFrom":subQ0}),1.0]])]});}
            var Q1;
            {var subQ0=sQuery(id+"F44.wireOp",EDGE,"E90.2");Q1=makeQuery(id+"F44.imprint","IMPRINT",FACE,{"disambiguationData":[TD([[makeQuery(id+"F44.imprint","IMPRINT",EDGE,{"derivedFrom":subQ0}),1.0]])]});}
            var Q2;
            {var subQ0=sQuery(id+"F44.wireOp",EDGE,"E90.1");Q2=makeQuery(id+"F44.imprint","IMPRINT",FACE,{"disambiguationData":[TD([[makeQuery(id+"F44.imprint","IMPRINT",EDGE,{"derivedFrom":subQ0}),1.0]])]});}
            var Q3;
            {var subQ0=sQuery(id+"F44.wireOp",EDGE,"E90.4");Q3=makeQuery(id+"F44.imprint","IMPRINT",FACE,{"disambiguationData":[TD([[makeQuery(id+"F44.imprint","IMPRINT",EDGE,{"derivedFrom":subQ0}),1.0]])]});}
            var Q4;
            {var subQ0=sQuery(id+"F44.wireOp",EDGE,"E90.7");Q4=makeQuery(id+"F44.imprint","IMPRINT",FACE,{"disambiguationData":[TD([[makeQuery(id+"F44.imprint","IMPRINT",EDGE,{"derivedFrom":subQ0}),1.0]])]});}
            var Q5;
            {var subQ0=sQuery(id+"F44.wireOp",EDGE,"E90.8");Q5=makeQuery(id+"F44.imprint","IMPRINT",FACE,{"disambiguationData":[TD([[makeQuery(id+"F44.imprint","IMPRINT",EDGE,{"derivedFrom":subQ0}),1.0]])]});}
            var Q6;
            {var subQ0=sQuery(id+"F44.wireOp",EDGE,"E90.9");Q6=makeQuery(id+"F44.imprint","IMPRINT",FACE,{"disambiguationData":[TD([[makeQuery(id+"F44.imprint","IMPRINT",EDGE,{"derivedFrom":subQ0}),1.0]])]});}
            var Q7;
            {var subQ0=sQuery(id+"F44.wireOp",EDGE,"E90.6");Q7=makeQuery(id+"F44.imprint","IMPRINT",FACE,{"disambiguationData":[TD([[makeQuery(id+"F44.imprint","IMPRINT",EDGE,{"derivedFrom":subQ0}),1.0]])]});}
            extrude(context, id + "F46", {"entities" : qUnion([Q0, Q1, Q2, Q3, Q4, Q5, Q6, Q7]), "operationType" : NewBodyOperationType.REMOVE, "oppositeDirection" : true, "depth" : 0.16 * mm, "offsetDistance" : 25 * mm});
        }
        {
            var Q0;
            {var subQ0=sQuery(id+"F0.wireOp",EDGE,"E0.top");var subQ2=sQuery(id+"F0.wireOp",EDGE,"E0.left");Q0=makeQuery(id+"F40.boolean.opBoolean","MERGE",FACE,{"derivedFrom":[makeQuery(id+"F21.boolean.opBoolean","SPLIT",FACE,{"disambiguationData":[TD([makeQuery(id+"F1.opExtrude","SWEPT_FACE",FACE,{"disambiguationData":[OSD([subQ2])]})])],"derivedFrom":makeQuery(id+"F1.opExtrude","SWEPT_FACE",FACE,{"disambiguationData":[OSD([subQ0])]})}),makeQuery(id+"F40.opExtrude","SWEPT_FACE",FACE,{"disambiguationData":[OSD([subQ0])]})]});}
            var sketch = newSketch(context, id + "F47", { "sketchPlane" : qUnion([Q0])});
            skCircle(sketch, "E91.0", {"center": v(-5.64, 6.9) * mm, "radius": 2.26 * mm});
            skCircle(sketch, "E91.1", {"center": v(-5.64, 6.9) * mm, "radius": 1.04 * mm});
            skCircle(sketch, "E92.0.1.0", {"center": v(-5.64, 19.1) * mm, "radius": 2.26 * mm});
            skCircle(sketch, "E92.0.1.1", {"center": v(-5.64, 19.1) * mm, "radius": 1.04 * mm});
            skCircle(sketch, "E92.1.0.0", {"center": v(8.24, 6.9) * mm, "radius": 2.26 * mm});
            skCircle(sketch, "E92.1.0.1", {"center": v(8.24, 6.9) * mm, "radius": 1.04 * mm});
            skCircle(sketch, "E92.1.1.0", {"center": v(8.24, 19.1) * mm, "radius": 2.26 * mm});
            skCircle(sketch, "E92.1.1.1", {"center": v(8.24, 19.1) * mm, "radius": 1.04 * mm});
            skLineSegment(sketch, "E92.direction1", {"start": v(-5.64, 6.9) * mm, "end": v(8.24, 6.9) * mm, "construction": true});
            skLineSegment(sketch, "E92.direction2", {"start": v(-5.64, 6.9) * mm, "end": v(-5.64, 19.1) * mm, "construction": true});
            skLineSegment(sketch, "E93", {"start": v(-12.61, 13) * mm, "end": v(15.28, 13) * mm, "construction": true});
            skPoint(sketch, "E94", {"position": v(-5.64, 13) * mm});
            skSolve(sketch);
        }
        {
            var Q0;
            Q0=qSketchRegion(id+"F47",true);
            extrude(context, id + "F48", {"entities" : qUnion([Q0]), "operationType" : NewBodyOperationType.ADD, "depth" : 3.78 * mm, "offsetDistance" : 25 * mm});
        }
        {
            var Q0;
            {var subQ0=sQuery(id+"F0.wireOp",EDGE,"E0.bottom");Q0=makeQuery(id+"F40.boolean.opBoolean","MERGE",FACE,{"derivedFrom":[makeQuery(id+"F1.opExtrude","SWEPT_FACE",FACE,{"disambiguationData":[OSD([subQ0])]}),makeQuery(id+"F40.opExtrude","SWEPT_FACE",FACE,{"disambiguationData":[OSD([subQ0])]})]});}
            var sketch = newSketch(context, id + "F49", { "sketchPlane" : qUnion([Q0])});
            skCircle(sketch, "E95.0", {"center": v(-8.23, 6.9) * mm, "radius": 2.53 * mm});
            skLineSegment(sketch, "E95.1", {"start": v(-10.48, 8.05) * mm, "end": v(-10.48, 5.74) * mm});
            skLineSegment(sketch, "E95.2", {"start": v(-7.08, 4.65) * mm, "end": v(-9.39, 4.65) * mm});
            skLineSegment(sketch, "E95.3", {"start": v(-5.98, 8.05) * mm, "end": v(-5.98, 5.74) * mm});
            skLineSegment(sketch, "E95.4", {"start": v(-7.08, 9.14) * mm, "end": v(-9.39, 9.14) * mm});
            skCircle(sketch, "E96.0.1.0", {"center": v(-8.23, 19.1) * mm, "radius": 2.53 * mm});
            skLineSegment(sketch, "E96.0.1.1", {"start": v(-7.08, 21.34) * mm, "end": v(-9.39, 21.34) * mm});
            skLineSegment(sketch, "E96.0.1.2", {"start": v(-10.48, 20.25) * mm, "end": v(-10.48, 17.94) * mm});
            skLineSegment(sketch, "E96.0.1.3", {"start": v(-7.08, 16.85) * mm, "end": v(-9.39, 16.85) * mm});
            skLineSegment(sketch, "E96.0.1.4", {"start": v(-5.98, 20.25) * mm, "end": v(-5.98, 17.94) * mm});
            skCircle(sketch, "E96.1.0.0", {"center": v(5.65, 6.9) * mm, "radius": 2.53 * mm});
            skLineSegment(sketch, "E96.1.0.1", {"start": v(6.8, 9.14) * mm, "end": v(4.5, 9.14) * mm});
            skLineSegment(sketch, "E96.1.0.2", {"start": v(3.4, 8.05) * mm, "end": v(3.4, 5.74) * mm});
            skLineSegment(sketch, "E96.1.0.3", {"start": v(6.8, 4.65) * mm, "end": v(4.5, 4.65) * mm});
            skLineSegment(sketch, "E96.1.0.4", {"start": v(7.9, 8.05) * mm, "end": v(7.9, 5.74) * mm});
            skCircle(sketch, "E96.1.1.0", {"center": v(5.65, 19.1) * mm, "radius": 2.53 * mm});
            skLineSegment(sketch, "E96.1.1.1", {"start": v(6.8, 21.34) * mm, "end": v(4.5, 21.34) * mm});
            skLineSegment(sketch, "E96.1.1.2", {"start": v(3.4, 20.25) * mm, "end": v(3.4, 17.94) * mm});
            skLineSegment(sketch, "E96.1.1.3", {"start": v(6.8, 16.85) * mm, "end": v(4.5, 16.85) * mm});
            skLineSegment(sketch, "E96.1.1.4", {"start": v(7.9, 20.25) * mm, "end": v(7.9, 17.94) * mm});
            skLineSegment(sketch, "E96.direction1", {"start": v(-8.23, 6.9) * mm, "end": v(5.65, 6.9) * mm, "construction": true});
            skLineSegment(sketch, "E96.direction2", {"start": v(-8.23, 6.9) * mm, "end": v(-8.23, 19.1) * mm, "construction": true});
            skLineSegment(sketch, "E97", {"start": v(-15.28, 13) * mm, "end": v(12.61, 13) * mm, "construction": true});
            skPoint(sketch, "E98", {"position": v(-8.23, 13) * mm});
            skSolve(sketch);
        }
        {
            var Q0;
            Q0=qSketchRegion(id+"F49",true);
            extrude(context, id + "F50", {"entities" : qUnion([Q0]), "operationType" : NewBodyOperationType.REMOVE, "oppositeDirection" : true, "depth" : 8.2 * mm, "offsetDistance" : 25 * mm});
        }
    });
